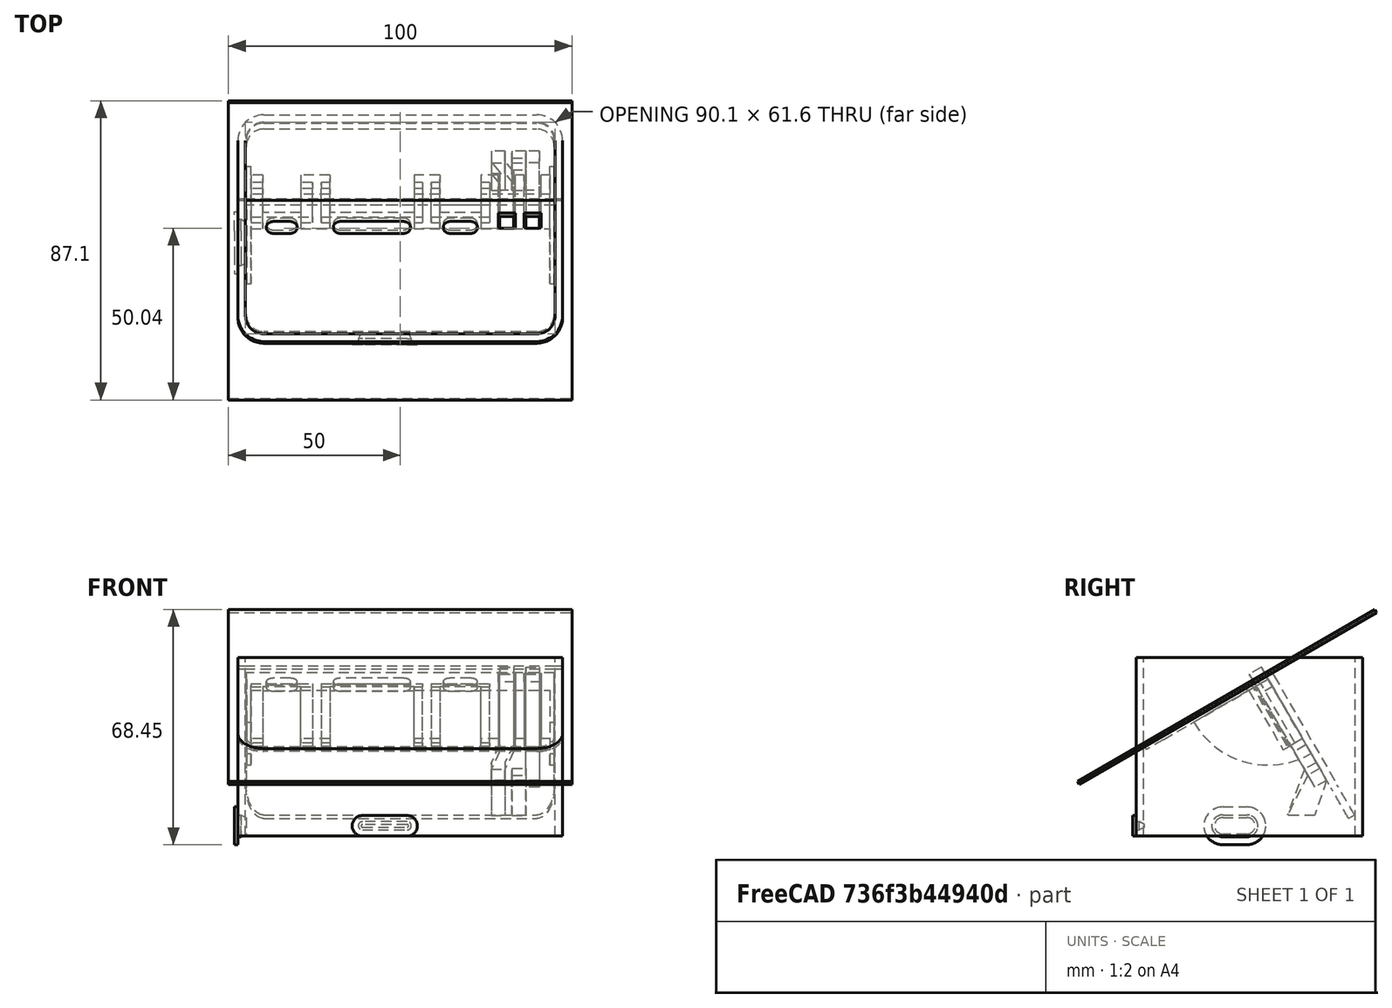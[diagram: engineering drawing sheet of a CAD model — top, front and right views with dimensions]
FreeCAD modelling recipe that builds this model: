
FCSTD DOCUMENT  (FreeCAD 0.21R33771 (Git))
Label: 2432S028_pins
License: All rights reserved
LicenseURL: http://en.wikipedia.org/wiki/All_rights_reserved
objects: Part::Extrusion×26, Sketcher::SketchObject×25, Part::FeaturePython×10, Part::Box×9, Part::Cut×7, Part::Chamfer×6, Mesh::Feature×6, Part::MultiCommon×1, Part::MultiFuse×1
note: 85 computed .brp shape members not serialized (recipe doc carries the construction recipe); baked Part::Feature solids carry a one-line shape summary decoded from their .brp

FEATURE [Sketcher::SketchObject] Sketch  label="Basis"
  FullyConstrained = true
  sketch-geometry (22):
    g0: LineSegment StartX=-39.75 StartY=33 StartZ=0 EndX=39.75 EndY=33 EndZ=0
    g1: LineSegment StartX=47.25 StartY=25.5 StartZ=0 EndX=47.25 EndY=-25.5 EndZ=0
    g2: LineSegment StartX=39.75 StartY=-33 StartZ=0 EndX=-39.75 EndY=-33 EndZ=0
    g3: LineSegment StartX=-47.25 StartY=-25.5 StartZ=0 EndX=-47.25 EndY=25.5 EndZ=0
    g4: ArcOfCircle CenterX=-39.75 CenterY=25.5 CenterZ=0 NormalX=0 NormalY=0 NormalZ=1 AngleXU=0 Radius=7.5 StartAngle=1.5708 EndAngle=3.14159
    g5: GeomPoint X=-47.25 Y=33 Z=0
    g6: ArcOfCircle CenterX=39.75 CenterY=25.5 CenterZ=0 NormalX=0 NormalY=0 NormalZ=1 AngleXU=0 Radius=7.5 StartAngle=0 EndAngle=1.5708
    g7: GeomPoint X=47.25 Y=33 Z=0
    g8: ArcOfCircle CenterX=39.75 CenterY=-25.5 CenterZ=0 NormalX=0 NormalY=0 NormalZ=1 AngleXU=0 Radius=7.5 StartAngle=4.71239 EndAngle=6.28319
    g9: GeomPoint X=47.25 Y=-33 Z=0
    g10: ArcOfCircle CenterX=-39.75 CenterY=-25.5 CenterZ=0 NormalX=0 NormalY=0 NormalZ=1 AngleXU=0 Radius=7.5 StartAngle=3.14159 EndAngle=4.71239
    g11: GeomPoint X=-47.25 Y=-33 Z=0
    g12: ArcOfCircle CenterX=39.75 CenterY=17.9 CenterZ=0 NormalX=0 NormalY=0 NormalZ=1 AngleXU=0 Radius=5.5 StartAngle=4e-16 EndAngle=1.5708
    g13: LineSegment StartX=45.25 StartY=17.9 StartZ=0 EndX=45.25 EndY=-25.5 EndZ=0
    g14: ArcOfCircle CenterX=39.75 CenterY=-25.5 CenterZ=0 NormalX=0 NormalY=0 NormalZ=1 AngleXU=0 Radius=5.5 StartAngle=4.71239 EndAngle=6.28319
    g15: LineSegment StartX=39.75 StartY=-31 StartZ=0 EndX=-39.75 EndY=-31 EndZ=0
    g16: ArcOfCircle CenterX=-39.75 CenterY=-25.5 CenterZ=0 NormalX=0 NormalY=0 NormalZ=1 AngleXU=0 Radius=5.5 StartAngle=3.14159 EndAngle=4.71239
    g17: LineSegment StartX=-45.25 StartY=-25.5 StartZ=0 EndX=-45.25 EndY=17.9 EndZ=0
    g18: ArcOfCircle CenterX=-39.75 CenterY=17.9 CenterZ=0 NormalX=0 NormalY=0 NormalZ=1 AngleXU=0 Radius=5.5 StartAngle=1.5708 EndAngle=3.14159
    g19: LineSegment StartX=-39.75 StartY=23.4 StartZ=0 EndX=39.75 EndY=23.4 EndZ=0
    g20: GeomPoint X=45.25 Y=23.4 Z=0
    g21: GeomPoint X=-45.25 Y=-31 Z=0
  constraints (50):
    c: Horizontal(g0)
    c: Horizontal(g2)
    c: Vertical(g1)
    c: Vertical(g3)
    c: DistanceY(g9,g7) = 66
    c: Symmetric(g5,g9,g-1)
    c: PointOnObject(g5,g0)
    c: PointOnObject(g5,g3)
    c: Tangent(g0,g4) = 1.5708
    c: Tangent(g3,g4) = 1.5708
    c: PointOnObject(g7,g0)
    c: PointOnObject(g7,g1)
    c: Tangent(g0,g6) = 1.5708
    c: Tangent(g1,g6) = 1.5708
    c: PointOnObject(g9,g1)
    c: PointOnObject(g9,g2)
    c: Tangent(g1,g8) = 1.5708
    c: Tangent(g2,g8) = 1.5708
    c: PointOnObject(g11,g2)
    c: PointOnObject(g11,g3)
    c: Tangent(g2,g10) = 1.5708
    c: Tangent(g3,g10) = 1.5708
    c: Equal(g8,g10)
    c: Equal(g10,g4)
    c: Equal(g4,g6)
    c: Tangent(g12,g13) = 1.5708
    c: Tangent(g13,g14) = 1.5708
    c: Tangent(g14,g15) = 1.5708
    c: Tangent(g15,g16) = 1.5708
    c: Tangent(g16,g17) = 1.5708
    c: Tangent(g17,g18) = 1.5708
    c: Tangent(g18,g19) = 1.5708
    c: Tangent(g19,g12) = 1.5708
    c: Horizontal(g15)
    c: Vertical(g13)
    c: Vertical(g17)
    c: Equal(g12,g14)
    c: Equal(g14,g16)
    c: Equal(g16,g18)
    c: PointOnObject(g20,g13)
    c: PointOnObject(g20,g19)
    c: PointOnObject(g21,g15)
    c: PointOnObject(g21,g17)
    c: DistanceY(g14,g12) = 54.4
    c: DistanceX(g17,g12) = 90.5
    c: Diameter(g12) = 11
    c: Symmetric(g12,g17,g-2)
    c: DistanceY(g2,g14) = 2
    c: Coincident(g10,g16)
    c: DistanceY(g18,g4) = 2.1
FEATURE [Part::Box] Box  label="Cube"
  AttacherType = Attacher::AttachEngine3D
  Height = 100
  Length = 100
  Placement = pos=(-50,39.3072,-0.4) rot=(1,0,0;0.523599rad)
  Width = 100
FEATURE [Sketcher::SketchObject] Sketch001
  ExternalGeometry = -> [Sketch]
  FullyConstrained = true
  sketch-geometry (20):
    g0: ArcOfCircle CenterX=-39.75 CenterY=25.5 CenterZ=0 NormalX=0 NormalY=0 NormalZ=1 AngleXU=0 Radius=7.5 StartAngle=1.5708 EndAngle=3.14159
    g1: LineSegment StartX=-39.75 StartY=33 StartZ=0 EndX=39.75 EndY=33 EndZ=0
    g2: ArcOfCircle CenterX=39.75 CenterY=25.5 CenterZ=0 NormalX=0 NormalY=0 NormalZ=1 AngleXU=0 Radius=7.5 StartAngle=1e-16 EndAngle=1.5708
    g3: LineSegment StartX=47.25 StartY=25.5 StartZ=0 EndX=47.25 EndY=-25.5 EndZ=0
    g4: ArcOfCircle CenterX=39.75 CenterY=-25.5 CenterZ=0 NormalX=0 NormalY=0 NormalZ=1 AngleXU=0 Radius=7.5 StartAngle=4.71239 EndAngle=6.28319
    g5: LineSegment StartX=39.75 StartY=-33 StartZ=0 EndX=-39.75 EndY=-33 EndZ=0
    g6: ArcOfCircle CenterX=-39.75 CenterY=-25.5 CenterZ=0 NormalX=0 NormalY=0 NormalZ=1 AngleXU=0 Radius=7.5 StartAngle=3.14159 EndAngle=4.71239
    g7: LineSegment StartX=-47.25 StartY=-25.5 StartZ=0 EndX=-47.25 EndY=25.5 EndZ=0
    g8: GeomPoint X=-47.25 Y=33 Z=0
    g9: GeomPoint X=47.25 Y=-33 Z=0
    g10: ArcOfCircle CenterX=-39.75 CenterY=17.9 CenterZ=0 NormalX=0 NormalY=0 NormalZ=1 AngleXU=0 Radius=5.5 StartAngle=1.5708 EndAngle=3.14159
    g11: LineSegment StartX=-39.75 StartY=23.4 StartZ=0 EndX=39.75 EndY=23.4 EndZ=0
    g12: ArcOfCircle CenterX=39.75 CenterY=17.9 CenterZ=0 NormalX=0 NormalY=0 NormalZ=1 AngleXU=0 Radius=5.5 StartAngle=0 EndAngle=1.5708
    g13: LineSegment StartX=45.25 StartY=17.9 StartZ=0 EndX=45.25 EndY=-25.5 EndZ=0
    g14: ArcOfCircle CenterX=39.75 CenterY=-25.5 CenterZ=0 NormalX=0 NormalY=0 NormalZ=1 AngleXU=0 Radius=5.5 StartAngle=4.71239 EndAngle=6.28319
    g15: LineSegment StartX=39.75 StartY=-31 StartZ=0 EndX=-39.75 EndY=-31 EndZ=0
    g16: ArcOfCircle CenterX=-39.75 CenterY=-25.5 CenterZ=0 NormalX=0 NormalY=0 NormalZ=1 AngleXU=0 Radius=5.5 StartAngle=3.14159 EndAngle=4.71239
    g17: LineSegment StartX=-45.25 StartY=-25.5 StartZ=0 EndX=-45.25 EndY=17.9 EndZ=0
    g18: GeomPoint X=-45.25 Y=23.4 Z=0
    g19: GeomPoint X=45.25 Y=-31 Z=0
  constraints (44):
    c: Tangent(g0,g1) = 1.5708
    c: Tangent(g1,g2) = 1.5708
    c: Tangent(g2,g3) = 1.5708
    c: Tangent(g3,g4) = 1.5708
    c: Tangent(g4,g5) = 1.5708
    c: Tangent(g5,g6) = 1.5708
    c: Tangent(g6,g7) = 1.5708
    c: Tangent(g7,g0) = 1.5708
    c: Horizontal(g1)
    c: Horizontal(g5)
    c: Vertical(g3)
    c: Vertical(g7)
    c: Equal(g0,g2)
    c: Equal(g2,g4)
    c: Equal(g4,g6)
    c: PointOnObject(g8,g1)
    c: PointOnObject(g8,g7)
    c: PointOnObject(g9,g3)
    c: PointOnObject(g9,g5)
    c: Coincident(g-6,g4)
    c: Coincident(g0,g-3)
    c: Horizontal(g-3,g0)
    c: Tangent(g10,g11) = 1.5708
    c: Tangent(g11,g12) = 1.5708
    c: Tangent(g12,g13) = 1.5708
    c: Tangent(g13,g14) = 1.5708
    c: Tangent(g14,g15) = 1.5708
    c: Tangent(g15,g16) = 1.5708
    c: Tangent(g16,g17) = 1.5708
    c: Tangent(g17,g10) = 1.5708
    c: Horizontal(g11)
    c: Horizontal(g15)
    c: Vertical(g13)
    c: Vertical(g17)
    c: Equal(g10,g12)
    c: Equal(g12,g14)
    c: Equal(g14,g16)
    c: PointOnObject(g18,g11)
    c: PointOnObject(g18,g17)
    c: PointOnObject(g19,g13)
    c: PointOnObject(g19,g15)
    c: Coincident(g14,g4)
    c: Coincident(g10,g-5)
    c: Horizontal(g-5,g10)
FEATURE [Part::Extrusion] Extrude
  Base = -> Sketch001
  Dir = (0,0,1)
  DirMode = 2
  FaceMakerClass = Part::FaceMakerBullseye
  LengthFwd = 2
  LengthRev = 0
  Solid = true
  Symmetric = false
FEATURE [Sketcher::SketchObject] Sketch002
  ExternalGeometry = -> [Sketch]
  FullyConstrained = true
  Placement = pos=(0,0,2) rot=(0,0,1;0rad)
  sketch-geometry (26):
    g0: ArcOfCircle CenterX=-39.75 CenterY=25.5 CenterZ=0 NormalX=0 NormalY=0 NormalZ=1 AngleXU=0 Radius=7.5 StartAngle=1.5708 EndAngle=3.14159
    g1: LineSegment StartX=-39.75 StartY=33 StartZ=0 EndX=39.75 EndY=33 EndZ=0
    g2: ArcOfCircle CenterX=39.75 CenterY=25.5 CenterZ=0 NormalX=0 NormalY=0 NormalZ=1 AngleXU=0 Radius=7.5 StartAngle=4e-16 EndAngle=1.5708
    g3: LineSegment StartX=47.25 StartY=25.5 StartZ=0 EndX=47.25 EndY=-25.5 EndZ=0
    g4: ArcOfCircle CenterX=39.75 CenterY=-25.5 CenterZ=0 NormalX=0 NormalY=0 NormalZ=1 AngleXU=0 Radius=7.5 StartAngle=4.71239 EndAngle=6.28319
    g5: LineSegment StartX=39.75 StartY=-33 StartZ=0 EndX=-39.75 EndY=-33 EndZ=0
    g6: ArcOfCircle CenterX=-39.75 CenterY=-25.5 CenterZ=0 NormalX=0 NormalY=0 NormalZ=1 AngleXU=0 Radius=7.5 StartAngle=3.14159 EndAngle=4.71239
    g7: LineSegment StartX=-47.25 StartY=-25.5 StartZ=0 EndX=-47.25 EndY=25.5 EndZ=0
    g8: GeomPoint X=-47.25 Y=33 Z=0
    g9: GeomPoint X=47.25 Y=-33 Z=0
    g10: ArcOfCircle CenterX=-39.75 CenterY=17.9 CenterZ=0 NormalX=0 NormalY=0 NormalZ=1 AngleXU=0 Radius=5.5 StartAngle=1.5708 EndAngle=3.14159
    g11: LineSegment StartX=-39.75 StartY=23.4 StartZ=0 EndX=39.75 EndY=23.4 EndZ=0
    g12: ArcOfCircle CenterX=39.75 CenterY=17.9 CenterZ=0 NormalX=0 NormalY=0 NormalZ=1 AngleXU=0 Radius=5.5 StartAngle=0 EndAngle=1.5708
    g13: LineSegment StartX=45.25 StartY=17.9 StartZ=0 EndX=45.25 EndY=-25.5 EndZ=0
    g14: ArcOfCircle CenterX=39.75 CenterY=-25.5 CenterZ=0 NormalX=0 NormalY=0 NormalZ=1 AngleXU=0 Radius=5.5 StartAngle=4.71239 EndAngle=6.28319
    g15: LineSegment StartX=39.75 StartY=-31 StartZ=0 EndX=-39.75 EndY=-31 EndZ=0
    g16: ArcOfCircle CenterX=-39.75 CenterY=-25.5 CenterZ=0 NormalX=0 NormalY=0 NormalZ=1 AngleXU=0 Radius=5.5 StartAngle=3.14159 EndAngle=4.71239
    g17: LineSegment StartX=-45.25 StartY=-25.5 StartZ=0 EndX=-45.25 EndY=17.9 EndZ=0
    g18: GeomPoint X=-45.25 Y=23.4 Z=0
    g19: GeomPoint X=45.25 Y=-31 Z=0
    g20: ArcOfCircle CenterX=-39.75 CenterY=25.5 CenterZ=0 NormalX=0 NormalY=0 NormalZ=1 AngleXU=0 Radius=5.5 StartAngle=1.5708 EndAngle=3.14159
    g21: LineSegment StartX=-39.75 StartY=31 StartZ=0 EndX=39.75 EndY=31 EndZ=0
    g22: ArcOfCircle CenterX=39.75 CenterY=25.5 CenterZ=0 NormalX=0 NormalY=0 NormalZ=1 AngleXU=0 Radius=5.5 StartAngle=0 EndAngle=1.5708
    g23: LineSegment StartX=-45.25 StartY=25.4 StartZ=0 EndX=45.25 EndY=25.4 EndZ=0
    g24: LineSegment StartX=-45.25 StartY=25.5 StartZ=0 EndX=-45.25 EndY=25.4 EndZ=0
    g25: LineSegment StartX=45.25 StartY=25.5 StartZ=0 EndX=45.25 EndY=25.4 EndZ=0
  constraints (62):
    c: Tangent(g0,g1) = 1.5708
    c: Tangent(g1,g2) = 1.5708
    c: Tangent(g2,g3) = 1.5708
    c: Tangent(g3,g4) = 1.5708
    c: Tangent(g4,g5) = 1.5708
    c: Tangent(g5,g6) = 1.5708
    c: Tangent(g6,g7) = 1.5708
    c: Tangent(g7,g0) = 1.5708
    c: Horizontal(g1)
    c: Horizontal(g5)
    c: Vertical(g3)
    c: Vertical(g7)
    c: Equal(g0,g2)
    c: Equal(g2,g4)
    c: Equal(g4,g6)
    c: PointOnObject(g8,g1)
    c: PointOnObject(g8,g7)
    c: PointOnObject(g9,g3)
    c: PointOnObject(g9,g5)
    c: Coincident(g4,g-6)
    c: Coincident(g0,g-3)
    c: Horizontal(g-3,g0)
    c: Tangent(g10,g11) = 1.5708
    c: Tangent(g11,g12) = 1.5708
    c: Tangent(g12,g13) = 1.5708
    c: Tangent(g13,g14) = 1.5708
    c: Tangent(g14,g15) = 1.5708
    c: Tangent(g15,g16) = 1.5708
    c: Tangent(g16,g17) = 1.5708
    c: Tangent(g17,g10) = 1.5708
    c: Horizontal(g11)
    c: Horizontal(g15)
    c: Vertical(g13)
    c: Vertical(g17)
    c: Equal(g10,g12)
    c: Equal(g12,g14)
    c: Equal(g14,g16)
    c: PointOnObject(g18,g11)
    c: PointOnObject(g18,g17)
    c: PointOnObject(g19,g13)
    c: PointOnObject(g19,g15)
    c: Coincident(g4,g14)
    c: Coincident(g10,g-5)
    c: Horizontal(g14,g-6)
    c: Coincident(g20,g0)
    c: Vertical(g0,g20)
    c: Horizontal(g0,g20)
    c: DistanceY(g20,g0) = 2
    c: Coincident(g21,g20)
    c: Horizontal(g21)
    c: Coincident(g22,g2)
    c: Coincident(g22,g21)
    c: Equal(g22,g20)
    c: Horizontal(g2,g22)
    c: Horizontal(g23)
    c: Coincident(g24,g20)
    c: Coincident(g24,g23)
    c: Vertical(g24)
    c: Coincident(g25,g22)
    c: Coincident(g25,g23)
    c: Vertical(g25)
    c: DistanceY(g10,g23) = 2
FEATURE [Part::Extrusion] Extrude001  label="Extrude_2mm"
  Base = -> Sketch002
  Dir = (0,0,1)
  DirMode = 2
  FaceMakerClass = Part::FaceMakerBullseye
  LengthFwd = 2
  LengthRev = 0
  Solid = true
  Symmetric = false
FEATURE [Sketcher::SketchObject] Sketch003
  ExternalGeometry = -> [Sketch]
  FullyConstrained = true
  Placement = pos=(0,0,4) rot=(0,0,1;0rad)
  sketch-geometry (20):
    g0: ArcOfCircle CenterX=-39.75 CenterY=25.5 CenterZ=0 NormalX=0 NormalY=0 NormalZ=1 AngleXU=0 Radius=7.5 StartAngle=1.5708 EndAngle=3.14159
    g1: LineSegment StartX=-39.75 StartY=33 StartZ=0 EndX=39.75 EndY=33 EndZ=0
    g2: ArcOfCircle CenterX=39.75 CenterY=25.5 CenterZ=0 NormalX=0 NormalY=0 NormalZ=1 AngleXU=0 Radius=7.5 StartAngle=0 EndAngle=1.5708
    g3: LineSegment StartX=47.25 StartY=25.5 StartZ=0 EndX=47.25 EndY=-25.5 EndZ=0
    g4: ArcOfCircle CenterX=39.75 CenterY=-25.5 CenterZ=0 NormalX=0 NormalY=0 NormalZ=1 AngleXU=0 Radius=7.5 StartAngle=4.71239 EndAngle=6.28319
    g5: LineSegment StartX=39.75 StartY=-33 StartZ=0 EndX=-39.75 EndY=-33 EndZ=0
    g6: ArcOfCircle CenterX=-39.75 CenterY=-25.5 CenterZ=0 NormalX=0 NormalY=0 NormalZ=1 AngleXU=0 Radius=7.5 StartAngle=3.14159 EndAngle=4.71239
    g7: LineSegment StartX=-47.25 StartY=-25.5 StartZ=0 EndX=-47.25 EndY=25.5 EndZ=0
    g8: GeomPoint X=-47.25 Y=33 Z=0
    g9: GeomPoint X=47.25 Y=-33 Z=0
    g10: ArcOfCircle CenterX=-39.75 CenterY=25.5 CenterZ=0 NormalX=0 NormalY=0 NormalZ=1 AngleXU=0 Radius=5.5 StartAngle=1.5708 EndAngle=3.14159
    g11: LineSegment StartX=-39.75 StartY=31 StartZ=0 EndX=39.75 EndY=31 EndZ=0
    g12: ArcOfCircle CenterX=39.75 CenterY=25.5 CenterZ=0 NormalX=0 NormalY=0 NormalZ=1 AngleXU=0 Radius=5.5 StartAngle=0 EndAngle=1.5708
    g13: LineSegment StartX=45.25 StartY=25.5 StartZ=0 EndX=45.25 EndY=-25.5 EndZ=0
    g14: ArcOfCircle CenterX=39.75 CenterY=-25.5 CenterZ=0 NormalX=0 NormalY=0 NormalZ=1 AngleXU=0 Radius=5.5 StartAngle=4.71239 EndAngle=6.28319
    g15: LineSegment StartX=39.75 StartY=-31 StartZ=0 EndX=-39.75 EndY=-31 EndZ=0
    g16: ArcOfCircle CenterX=-39.75 CenterY=-25.5 CenterZ=0 NormalX=0 NormalY=0 NormalZ=1 AngleXU=0 Radius=5.5 StartAngle=3.14159 EndAngle=4.71239
    g17: LineSegment StartX=-45.25 StartY=-25.5 StartZ=0 EndX=-45.25 EndY=25.5 EndZ=0
    g18: GeomPoint X=-45.25 Y=31 Z=0
    g19: GeomPoint X=45.25 Y=-31 Z=0
  constraints (45):
    c: Tangent(g0,g1) = 1.5708
    c: Tangent(g1,g2) = 1.5708
    c: Tangent(g2,g3) = 1.5708
    c: Tangent(g3,g4) = 1.5708
    c: Tangent(g4,g5) = 1.5708
    c: Tangent(g5,g6) = 1.5708
    c: Tangent(g6,g7) = 1.5708
    c: Tangent(g7,g0) = 1.5708
    c: Horizontal(g1)
    c: Horizontal(g5)
    c: Vertical(g3)
    c: Vertical(g7)
    c: Equal(g0,g2)
    c: Equal(g2,g4)
    c: Equal(g4,g6)
    c: PointOnObject(g8,g1)
    c: PointOnObject(g8,g7)
    c: PointOnObject(g9,g3)
    c: PointOnObject(g9,g5)
    c: Coincident(g-5,g4)
    c: Coincident(g0,g-3)
    c: Horizontal(g-3,g0)
    c: Tangent(g10,g11) = 1.5708
    c: Tangent(g12,g13) = 1.5708
    c: Tangent(g13,g14) = 1.5708
    c: Tangent(g14,g15) = 1.5708
    c: Tangent(g15,g16) = 1.5708
    c: Tangent(g16,g17) = 1.5708
    c: Tangent(g17,g10) = 1.5708
    c: Horizontal(g11)
    c: Horizontal(g15)
    c: Vertical(g13)
    c: Vertical(g17)
    c: Equal(g10,g12)
    c: Equal(g12,g14)
    c: Equal(g14,g16)
    c: PointOnObject(g18,g11)
    c: PointOnObject(g18,g17)
    c: PointOnObject(g19,g13)
    c: PointOnObject(g19,g15)
    c: Coincident(g14,g4)
    c: Coincident(g11,g12)
    c: Coincident(g0,g10)
    c: Horizontal(g15,g-6)
    c: Vertical(g12,g11)
FEATURE [Part::Extrusion] Extrude002  label="Extrude_4mm"
  Base = -> Sketch003
  Dir = (0,0,1)
  DirMode = 2
  FaceMakerClass = Part::FaceMakerBullseye
  LengthFwd = 10
  LengthRev = 0
  Solid = true
  Symmetric = false
FEATURE [Part::Extrusion] Extrude003  label="Extrude_6mm"
  Base = -> Sketch003
  Dir = (0,0,1)
  DirMode = 2
  FaceMakerClass = Part::FaceMakerBullseye
  LengthFwd = 52
  LengthRev = 0
  Solid = true
  Symmetric = false
FEATURE [Part::Box] Box001  label="Cube001"
  AttacherType = Attacher::AttachEngine3D
  Height = 100
  Length = 100
  Placement = pos=(-50,-49.5397,19.0874) rot=(1,0,0;0.523599rad)
  Width = 100
FEATURE [Part::Box] Box002  label="Cube002"
  AttacherType = Attacher::AttachEngine3D
  Height = 100
  Length = 100
  Placement = pos=(-50,37.5751,-1.4) rot=(1,0,0;0.523599rad)
  Width = 2
FEATURE [Sketcher::SketchObject] Sketch004
  ExternalGeometry = -> [Sketch]
  FullyConstrained = false
  sketch-geometry (12):
    g0: ArcOfCircle CenterX=-39.75 CenterY=25.5 CenterZ=0 NormalX=0 NormalY=0 NormalZ=1 AngleXU=0 Radius=7.5 StartAngle=1.5708 EndAngle=3.14159
    g1: LineSegment StartX=-39.75 StartY=33 StartZ=0 EndX=39.75 EndY=33 EndZ=0
    g2: ArcOfCircle CenterX=39.75 CenterY=25.5 CenterZ=0 NormalX=0 NormalY=0 NormalZ=1 AngleXU=0 Radius=7.5 StartAngle=1e-16 EndAngle=1.5708
    g3: LineSegment StartX=47.25 StartY=25.5 StartZ=0 EndX=47.25 EndY=-25.5 EndZ=0
    g4: ArcOfCircle CenterX=39.75 CenterY=-25.5 CenterZ=0 NormalX=0 NormalY=0 NormalZ=1 AngleXU=0 Radius=7.5 StartAngle=4.71239 EndAngle=6.28319
    g5: LineSegment StartX=39.75 StartY=-33 StartZ=0 EndX=-39.75 EndY=-33 EndZ=0
    g6: ArcOfCircle CenterX=-39.75 CenterY=-25.5 CenterZ=0 NormalX=0 NormalY=0 NormalZ=1 AngleXU=0 Radius=7.5 StartAngle=3.14159 EndAngle=4.71239
    g7: LineSegment StartX=-47.25 StartY=-25.5 StartZ=0 EndX=-47.25 EndY=25.5 EndZ=0
    g8: GeomPoint X=-47.25 Y=33 Z=0
    g9: GeomPoint X=47.25 Y=-33 Z=0
    g10: GeomPoint X=-22 Y=14 Z=0
    g11: GeomPoint X=22 Y=-30 Z=0
  constraints (22):
    c: Tangent(g0,g1) = 1.5708
    c: Tangent(g1,g2) = 1.5708
    c: Tangent(g2,g3) = 1.5708
    c: Tangent(g3,g4) = 1.5708
    c: Tangent(g4,g5) = 1.5708
    c: Tangent(g5,g6) = 1.5708
    c: Tangent(g6,g7) = 1.5708
    c: Tangent(g7,g0) = 1.5708
    c: Horizontal(g1)
    c: Horizontal(g5)
    c: Vertical(g3)
    c: Vertical(g7)
    c: Equal(g0,g2)
    c: Equal(g2,g4)
    c: Equal(g4,g6)
    c: PointOnObject(g8,g1)
    c: PointOnObject(g8,g7)
    c: PointOnObject(g9,g3)
    c: PointOnObject(g9,g5)
    c: Coincident(g0,g-3)
    c: Horizontal(g-3,g0)
    c: Coincident(g4,g-4)
FEATURE [Part::Extrusion] Extrude004
  Base = -> Sketch004
  Dir = (0,0,1)
  DirMode = 2
  FaceMakerClass = Part::FaceMakerBullseye
  LengthFwd = 56
  LengthRev = 0
  Solid = true
  Symmetric = false
FEATURE [Part::MultiCommon] Common
  Shapes = -> [Box002,Extrude004]
FEATURE [Part::MultiFuse] Fusion
  Shapes = -> [Common,Extrude,Extrude001,Extrude002,Extrude003]
FEATURE [Part::Cut] Cut
  Base = -> Fusion
  Tool = -> Box
FEATURE [Part::Cut] Cut001
  Base = -> Cut
  Tool = -> Box001
FEATURE [Part::Box] Box003  label="Cube003"
  AttacherType = Attacher::AttachEngine3D
  Height = 3
  Length = 1.5
  Placement = pos=(43.75,-29,7) rot=(0,0,1;0rad)
  Width = 14.7
FEATURE [Part::Chamfer] Chamfer
  Base = -> Box003
  Edges = 4 edges r=1.49: [Edge1,Edge2,Edge3,Edge4]
FEATURE [Part::Box] Box004  label="Cube004"
  AttacherType = Attacher::AttachEngine3D
  Height = 3
  Length = 1.5
  Placement = pos=(-45.25,-29,8) rot=(0,0,1;0rad)
  Width = 14.7
FEATURE [Part::Chamfer] Chamfer001
  Base = -> Box004
  Edges = 4 edges r=1.49: [Edge5,Edge6,Edge7,Edge8]
FEATURE [Sketcher::SketchObject] Sketch005  label="Basis001_bEZEL"
  FullyConstrained = true
  Placement = pos=(0,-2.75,0) rot=(0,1,0;3.14159rad)
  sketch-geometry (46):
    g0: ArcOfCircle CenterX=40 CenterY=22 CenterZ=0 NormalX=0 NormalY=0 NormalZ=1 AngleXU=0 Radius=3 StartAngle=4e-16 EndAngle=1.5708
    g1: LineSegment StartX=43 StartY=22 StartZ=0 EndX=43 EndY=-22 EndZ=0
    g2: ArcOfCircle CenterX=40 CenterY=-22 CenterZ=0 NormalX=0 NormalY=0 NormalZ=1 AngleXU=0 Radius=3 StartAngle=4.71239 EndAngle=6.28319
    g3: LineSegment StartX=40 StartY=-25 StartZ=0 EndX=-40 EndY=-25 EndZ=0
    g4: ArcOfCircle CenterX=-40 CenterY=-22 CenterZ=0 NormalX=0 NormalY=0 NormalZ=1 AngleXU=0 Radius=3 StartAngle=3.14159 EndAngle=4.71239
    g5: LineSegment StartX=-43 StartY=-22 StartZ=0 EndX=-43 EndY=22 EndZ=0
    g6: ArcOfCircle CenterX=-40 CenterY=22 CenterZ=0 NormalX=0 NormalY=0 NormalZ=1 AngleXU=0 Radius=3 StartAngle=1.5708 EndAngle=3.14159
    g7: LineSegment StartX=-40 StartY=25 StartZ=0 EndX=40 EndY=25 EndZ=0
    g8: GeomPoint X=43 Y=25 Z=0
    g9: GeomPoint X=-43 Y=-25 Z=0
    g10: Circle CenterX=-39 CenterY=21 CenterZ=0 NormalX=0 NormalY=0 NormalZ=1 AngleXU=0 Radius=1.6
    g11: Circle CenterX=-39 CenterY=-21 CenterZ=0 NormalX=0 NormalY=0 NormalZ=1 AngleXU=0 Radius=1.6
    g12: Circle CenterX=39 CenterY=21 CenterZ=0 NormalX=0 NormalY=0 NormalZ=1 AngleXU=0 Radius=1.6
    g13: Circle CenterX=39 CenterY=-21 CenterZ=0 NormalX=0 NormalY=0 NormalZ=1 AngleXU=0 Radius=1.6
    g14: LineSegment StartX=-35 StartY=25 StartZ=0 EndX=36 EndY=25 EndZ=0
    g15: LineSegment StartX=36 StartY=25 StartZ=0 EndX=36 EndY=-25 EndZ=0
    g16: LineSegment StartX=36 StartY=-25 StartZ=0 EndX=-35 EndY=-25 EndZ=0
    g17: LineSegment StartX=-35 StartY=-25 StartZ=0 EndX=-35 EndY=25 EndZ=0
    g18: LineSegment StartX=-40.4 StartY=-12 StartZ=0 EndX=-37.4 EndY=-12 EndZ=0
    g19: LineSegment StartX=-37.4 StartY=-12 StartZ=0 EndX=-37.4 EndY=-17 EndZ=0
    g20: LineSegment StartX=-37.4 StartY=-17 StartZ=0 EndX=-40.4 EndY=-17 EndZ=0
    g21: LineSegment StartX=-40.4 StartY=-17 StartZ=0 EndX=-40.4 EndY=-12 EndZ=0
    g22: LineSegment StartX=-2 StartY=-25 StartZ=0 EndX=11 EndY=-25 EndZ=0
    g23: LineSegment StartX=11 StartY=-25 StartZ=0 EndX=11 EndY=-28 EndZ=0
    g24: LineSegment StartX=11 StartY=-28 StartZ=0 EndX=-2 EndY=-28 EndZ=0
    g25: LineSegment StartX=-2 StartY=-28 StartZ=0 EndX=-2 EndY=-25 EndZ=0
    g26: LineSegment StartX=43 StartY=3 StartZ=0 EndX=53 EndY=3 EndZ=0
    g27: LineSegment StartX=53 StartY=3 StartZ=0 EndX=53 EndY=-6 EndZ=0
    g28: LineSegment StartX=53 StartY=-6 StartZ=0 EndX=43 EndY=-6 EndZ=0
    g29: LineSegment StartX=43 StartY=-6 StartZ=0 EndX=43 EndY=3 EndZ=0
    g30: LineSegment StartX=43 StartY=14 StartZ=0 EndX=45 EndY=14 EndZ=0
    g31: LineSegment StartX=45 StartY=14 StartZ=0 EndX=45 EndY=6 EndZ=0
    g32: LineSegment StartX=45 StartY=6 StartZ=0 EndX=43 EndY=6 EndZ=0
    g33: LineSegment StartX=43 StartY=6 StartZ=0 EndX=43 EndY=14 EndZ=0
    g34: LineSegment StartX=-31.5 StartY=-25 StartZ=0 EndX=-23.5 EndY=-25 EndZ=0
    g35: LineSegment StartX=-23.5 StartY=-25 StartZ=0 EndX=-23.5 EndY=-27 EndZ=0
    g36: LineSegment StartX=-23.5 StartY=-27 StartZ=0 EndX=-31.5 EndY=-27 EndZ=0
    g37: LineSegment StartX=-31.5 StartY=-27 StartZ=0 EndX=-31.5 EndY=-25 EndZ=0
    g38: LineSegment StartX=-16.5 StartY=-25 StartZ=0 EndX=-8.5 EndY=-25 EndZ=0
    g39: LineSegment StartX=-8.5 StartY=-25 StartZ=0 EndX=-8.5 EndY=-27 EndZ=0
    g40: LineSegment StartX=-8.5 StartY=-27 StartZ=0 EndX=-16.5 EndY=-27 EndZ=0
    g41: LineSegment StartX=-16.5 StartY=-27 StartZ=0 EndX=-16.5 EndY=-25 EndZ=0
    g42: LineSegment StartX=-33 StartY=22.5 StartZ=0 EndX=27 EndY=22.5 EndZ=0
    g43: LineSegment StartX=27 StartY=22.5 StartZ=0 EndX=27 EndY=-22.5 EndZ=0
    g44: LineSegment StartX=27 StartY=-22.5 StartZ=0 EndX=-33 EndY=-22.5 EndZ=0
    g45: LineSegment StartX=-33 StartY=-22.5 StartZ=0 EndX=-33 EndY=22.5 EndZ=0
  constraints (130):
    c: Tangent(g0,g1) = 1.5708
    c: Tangent(g1,g2) = 1.5708
    c: Tangent(g2,g3) = 1.5708
    c: Tangent(g3,g4) = 1.5708
    c: Tangent(g4,g5) = 1.5708
    c: Tangent(g5,g6) = 1.5708
    c: Tangent(g6,g7) = 1.5708
    c: Tangent(g7,g0) = 1.5708
    c: Horizontal(g3)
    c: Vertical(g1)
    c: Vertical(g5)
    c: Equal(g0,g2)
    c: Equal(g2,g4)
    c: Equal(g4,g6)
    c: PointOnObject(g8,g1)
    c: PointOnObject(g8,g7)
    c: PointOnObject(g9,g3)
    c: PointOnObject(g9,g5)
    c: DistanceY(g2,g0) = 50
    c: DistanceX(g5,g0) = 86
    c: Diameter(g0) = 6
    c: Symmetric(g6,g2,g-1)
    c: Horizontal(g7)
    c: Diameter(g10) = 3.2
    c: DistanceY(g10,g6) = 4
    c: DistanceX(g5,g10) = 4
    c: Equal(g10,g12)
    c: Horizontal(g10,g12)
    c: Vertical(g10,g11)
    c: Horizontal(g11,g13)
    c: Vertical(g13,g12)
    c: Equal(g10,g11)
    c: Equal(g11,g13)
    c: DistanceY(g2,g13) = 4
    c: DistanceX(g13,g1) = 4
    c: Coincident(g14,g15)
    c: Coincident(g15,g16)
    c: Coincident(g16,g17)
    c: Coincident(g17,g14)
    c: Horizontal(g14)
    c: Horizontal(g16)
    c: Vertical(g15)
    c: Vertical(g17)
    c: PointOnObject(g14,g7)
    c: PointOnObject(g16,g3)
    c: DistanceX(g14,g0) = 7
    c: DistanceX(g5,g14) = 8
    c: Coincident(g18,g19)
    c: Coincident(g19,g20)
    c: Coincident(g20,g21)
    c: Coincident(g21,g18)
    c: Horizontal(g18)
    c: Horizontal(g20)
    c: Vertical(g19)
    c: Vertical(g21)
    c: DistanceX(g20,g20) = 3
    c: DistanceY(g21,g21) = 5
    c: DistanceY(g3,g20) = 8
    c: DistanceX(g4,g20) = 2.6
    c: Coincident(g22,g23)
    c: Coincident(g23,g24)
    c: Coincident(g24,g25)
    c: Coincident(g25,g22)
    c: Horizontal(g22)
    c: Horizontal(g24)
    c: Vertical(g23)
    c: Vertical(g25)
    c: PointOnObject(g22,g3)
    c: DistanceX(g4,g22) = 41
    c: DistanceX(g22,g1) = 32
    c: DistanceY(g23,g23) = 3
    c: Coincident(g26,g27)
    c: Coincident(g27,g28)
    c: Coincident(g28,g29)
    c: Coincident(g29,g26)
    c: Horizontal(g26)
    c: Horizontal(g28)
    c: Vertical(g27)
    c: Vertical(g29)
    c: PointOnObject(g26,g1)
    c: DistanceY(g26,g0) = 22
    c: DistanceY(g2,g28) = 19
    c: DistanceX(g26,g26) = 10
    c: Coincident(g30,g31)
    c: Coincident(g31,g32)
    c: Coincident(g32,g33)
    c: Coincident(g33,g30)
    c: Horizontal(g30)
    c: Horizontal(g32)
    c: Vertical(g31)
    c: Vertical(g33)
    c: PointOnObject(g30,g1)
    c: DistanceY(g30,g0) = 11
    c: DistanceY(g2,g32) = 31
    c: DistanceX(g30,g30) = 2
    c: Coincident(g34,g35)
    c: Coincident(g35,g36)
    c: Coincident(g36,g37)
    c: Coincident(g37,g34)
    c: Horizontal(g34)
    c: Horizontal(g36)
    c: Vertical(g35)
    c: Vertical(g37)
    c: PointOnObject(g34,g3)
    c: Coincident(g38,g39)
    c: Coincident(g39,g40)
    c: Coincident(g40,g41)
    c: Coincident(g41,g38)
    c: Horizontal(g38)
    c: Horizontal(g40)
    c: Vertical(g39)
    c: Vertical(g41)
    c: PointOnObject(g38,g3)
    c: Equal(g31,g40)
    c: Equal(g40,g36)
    c: Equal(g32,g39)
    c: Equal(g39,g35)
    c: DistanceX(g4,g34) = 11.5
    c: DistanceX(g4,g38) = 26.5
    c: Coincident(g42,g43)
    c: Coincident(g43,g44)
    c: Coincident(g44,g45)
    c: Coincident(g45,g42)
    c: Horizontal(g42)
    c: Horizontal(g44)
    c: Vertical(g43)
    c: DistanceX(g44,g44) = 60
    c: DistanceY(g43,g43) = 45
    c: Symmetric(g42,g44,g-1)
    c: DistanceX(g14,g42) = 2
FEATURE [Sketcher::SketchObject] Sketch006
  ExternalGeometry = -> [Sketch005]
  FullyConstrained = true
  MapMode = 5
  Placement = pos=(0,-33,0) rot=(1,0,0;1.5708rad)
  Support = -> [Cut001]
  sketch-geometry (4):
    g0: ArcOfCircle CenterX=2 CenterY=7 CenterZ=0 NormalX=0 NormalY=0 NormalZ=1 AngleXU=0 Radius=1.5 StartAngle=4.71239 EndAngle=7.85398
    g1: ArcOfCircle CenterX=-11 CenterY=7 CenterZ=0 NormalX=0 NormalY=0 NormalZ=1 AngleXU=0 Radius=1.5 StartAngle=1.5708 EndAngle=4.71239
    g2: LineSegment StartX=2 StartY=8.5 StartZ=0 EndX=-11 EndY=8.5 EndZ=0
    g3: LineSegment StartX=-11 StartY=5.5 StartZ=0 EndX=2 EndY=5.5 EndZ=0
  constraints (10):
    c: Tangent(g0,g2) = -1.5708
    c: Tangent(g2,g1) = -1.5708
    c: Tangent(g1,g3) = -1.5708
    c: Tangent(g3,g0) = -1.5708
    c: Equal(g0,g1)
    c: Horizontal(g2)
    c: DistanceY(g-1,g1) = 7
    c: Diameter(g1) = 3
    c: Vertical(g1,g-3)
    c: Vertical(g0,g-3)
FEATURE [Part::Extrusion] Extrude005
  Base = -> Sketch006
  Dir = (0,-1,2e-16)
  DirMode = 2
  FaceMakerClass = Part::FaceMakerBullseye
  LengthFwd = 3
  LengthRev = 0
  Reversed = true
  Solid = true
  Symmetric = false
FEATURE [Sketcher::SketchObject] Sketch007
  ExternalGeometry = -> [Sketch005]
  FullyConstrained = true
  MapMode = 5
  Placement = pos=(-47.25,0,0) rot=(0.57735,-0.57735,-0.57735;2.0944rad)
  Support = -> [Cut001]
  sketch-geometry (6):
    g0: ArcOfCircle CenterX=0.75 CenterY=7 CenterZ=0 NormalX=0 NormalY=0 NormalZ=1 AngleXU=0 Radius=3.5 StartAngle=1.5708 EndAngle=4.71239
    g1: ArcOfCircle CenterX=7.75 CenterY=7 CenterZ=0 NormalX=0 NormalY=0 NormalZ=1 AngleXU=0 Radius=3.5 StartAngle=4.71239 EndAngle=7.85398
    g2: LineSegment StartX=0.75 StartY=3.5 StartZ=0 EndX=7.75 EndY=3.5 EndZ=0
    g3: LineSegment StartX=7.75 StartY=10.5 StartZ=0 EndX=0.75 EndY=10.5 EndZ=0
    g4: LineSegment StartX=-0.25 StartY=-6.5e-15 StartZ=0 EndX=0.75 EndY=3.5 EndZ=0
    g5: LineSegment StartX=7.75 StartY=3.5 StartZ=0 EndX=8.75 EndY=-6.7e-15 EndZ=0
  constraints (14):
    c: Tangent(g0,g2) = -1.5708
    c: Tangent(g2,g1) = -1.5708
    c: Tangent(g1,g3) = -1.5708
    c: Tangent(g3,g0) = -1.5708
    c: Equal(g0,g1)
    c: Horizontal(g2)
    c: DistanceY(g-1,g1) = 7
    c: Diameter(g1) = 7
    c: DistanceX(g3,g3) = 7
    c: Coincident(g4,g-3)
    c: Coincident(g4,g0)
    c: Coincident(g5,g1)
    c: Coincident(g5,g-3)
    c: Equal(g5,g4)
FEATURE [Part::Extrusion] Extrude006
  Base = -> Sketch007
  Dir = (-1,0,0)
  DirMode = 2
  FaceMakerClass = Part::FaceMakerBullseye
  LengthFwd = 3
  LengthRev = 0
  Reversed = true
  Solid = true
  Symmetric = false
FEATURE [Part::Box] Box005  label="Cube005"
  AttacherType = Attacher::AttachEngine3D
  Height = 3
  Length = 1.5
  Placement = pos=(43.75,10,7) rot=(0,0,1;0rad)
  Width = 14.7
FEATURE [Part::Chamfer] Chamfer002
  Base = -> Box005
  Edges = 4 edges r=1.49: [Edge1,Edge2,Edge3,Edge4]
FEATURE [Part::Box] Box006  label="Cube006"
  AttacherType = Attacher::AttachEngine3D
  Height = 3
  Length = 1.5
  Placement = pos=(-45.25,10,8) rot=(0,0,1;0rad)
  Width = 14.7
FEATURE [Part::Chamfer] Chamfer003
  Base = -> Box006
  Edges = 4 edges r=1.49: [Edge5,Edge6,Edge7,Edge8]
FEATURE [Part::Cut] Cut002
  Base = -> Cut001
  Tool = -> Extrude005
FEATURE [Part::Cut] Cut003
  Base = -> Cut002
  Tool = -> Extrude006
FEATURE [Part::FeaturePython] Connect  label="Main"  # WARN: FeaturePython — macro-defined, semantics opaque (R4)
  Objects = -> [Chamfer,Chamfer001,Chamfer002,Chamfer003,Cut003]
  Tolerance = 0
FEATURE [Mesh::Feature] Mesh  label="Main (Meshed)"
FEATURE [Sketcher::SketchObject] Sketch008
  ExternalGeometry = -> [Sketch007]
  FullyConstrained = true
  MapMode = 2
  Placement = pos=(-47.25,0,0) rot=(0.57735,-0.57735,-0.57735;2.0944rad)
  Support = -> [Sketch007]
  sketch-geometry (4):
    g0: ArcOfCircle CenterX=0.75 CenterY=7 CenterZ=0 NormalX=0 NormalY=0 NormalZ=1 AngleXU=0 Radius=3.2 StartAngle=1.5708 EndAngle=4.71239
    g1: ArcOfCircle CenterX=7.75 CenterY=7 CenterZ=0 NormalX=0 NormalY=0 NormalZ=1 AngleXU=0 Radius=3.2 StartAngle=4.71239 EndAngle=7.85398
    g2: LineSegment StartX=0.75 StartY=3.8 StartZ=0 EndX=7.75 EndY=3.8 EndZ=0
    g3: LineSegment StartX=7.75 StartY=10.2 StartZ=0 EndX=0.75 EndY=10.2 EndZ=0
  constraints (9):
    c: Radius(g-3) = 3.5
    c: Tangent(g0,g2) = -1.5708
    c: Tangent(g2,g1) = -1.5708
    c: Tangent(g1,g3) = -1.5708
    c: Tangent(g3,g0) = -1.5708
    c: Equal(g0,g1)
    c: Coincident(g0,g-3)
    c: Coincident(g1,g-4)
    c: Radius(g0) = 3.2
FEATURE [Part::Extrusion] Extrude007
  Base = -> Sketch008
  Dir = (-1,0,0)
  DirMode = 2
  FaceMakerClass = Part::FaceMakerBullseye
  LengthFwd = 2.4
  LengthRev = 0
  Reversed = true
  Solid = true
  Symmetric = false
FEATURE [Part::Chamfer] Chamfer004
  Base = -> Extrude007
  Edges = 1 edges: [Edge7 r1=1.5 r2=0.8]
FEATURE [Sketcher::SketchObject] Sketch009
  ExternalGeometry = -> [Sketch007]
  FullyConstrained = true
  MapMode = 2
  Placement = pos=(-47.25,0,0) rot=(0.57735,-0.57735,-0.57735;2.0944rad)
  Support = -> [Sketch007]
  sketch-geometry (4):
    g0: ArcOfCircle CenterX=0.75 CenterY=7 CenterZ=0 NormalX=0 NormalY=0 NormalZ=1 AngleXU=0 Radius=5.5 StartAngle=1.5708 EndAngle=4.71239
    g1: ArcOfCircle CenterX=7.75 CenterY=7 CenterZ=0 NormalX=0 NormalY=0 NormalZ=1 AngleXU=0 Radius=5.5 StartAngle=4.71239 EndAngle=7.85398
    g2: LineSegment StartX=0.75 StartY=1.5 StartZ=0 EndX=7.75 EndY=1.5 EndZ=0
    g3: LineSegment StartX=7.75 StartY=12.5 StartZ=0 EndX=0.75 EndY=12.5 EndZ=0
  constraints (9):
    c: Radius(g-3) = 3.5
    c: Tangent(g0,g2) = -1.5708
    c: Tangent(g2,g1) = -1.5708
    c: Tangent(g1,g3) = -1.5708
    c: Tangent(g3,g0) = -1.5708
    c: Equal(g0,g1)
    c: Coincident(g0,g-3)
    c: Coincident(g1,g-4)
    c: Radius(g0) = 5.5
FEATURE [Part::Extrusion] Extrude008
  Base = -> Sketch009
  Dir = (-1,0,0)
  DirMode = 2
  FaceMakerClass = Part::FaceMakerBullseye
  LengthFwd = 1
  LengthRev = 0
  Solid = true
  Symmetric = false
FEATURE [Part::FeaturePython] Connect001  label="Deckel_USB"  # WARN: FeaturePython — macro-defined, semantics opaque (R4)
  Objects = -> [Chamfer004,Extrude008]
  Tolerance = 0
FEATURE [Mesh::Feature] Mesh001  label="Deckel_USB (Meshed)"
  Placement = pos=(-57.5,0,48.25) rot=(0,1,0;4.71239rad)
FEATURE [Sketcher::SketchObject] Sketch010
  ExternalGeometry = -> [Sketch006]
  FullyConstrained = true
  MapMode = 2
  Placement = pos=(0,-33,0) rot=(1,0,0;1.5708rad)
  Support = -> [Sketch006]
  sketch-geometry (4):
    g0: ArcOfCircle CenterX=-11 CenterY=7 CenterZ=0 NormalX=0 NormalY=0 NormalZ=1 AngleXU=0 Radius=1.2 StartAngle=1.5708 EndAngle=4.71239
    g1: ArcOfCircle CenterX=2 CenterY=7 CenterZ=0 NormalX=0 NormalY=0 NormalZ=1 AngleXU=0 Radius=1.2 StartAngle=4.71239 EndAngle=7.85398
    g2: LineSegment StartX=-11 StartY=5.8 StartZ=0 EndX=2 EndY=5.8 EndZ=0
    g3: LineSegment StartX=2 StartY=8.2 StartZ=0 EndX=-11 EndY=8.2 EndZ=0
  constraints (9):
    c: Tangent(g0,g2) = -1.5708
    c: Tangent(g2,g1) = -1.5708
    c: Tangent(g1,g3) = -1.5708
    c: Tangent(g3,g0) = -1.5708
    c: Equal(g0,g1)
    c: Coincident(g0,g-3)
    c: Coincident(g1,g-4)
    c: Radius(g-3) = 1.5
    c: Radius(g0) = 1.2
FEATURE [Part::Extrusion] Extrude009
  Base = -> Sketch010
  Dir = (0,-1,2e-16)
  DirMode = 2
  FaceMakerClass = Part::FaceMakerBullseye
  LengthFwd = 2.4
  LengthRev = 0
  Reversed = true
  Solid = true
  Symmetric = false
FEATURE [Sketcher::SketchObject] Sketch011
  ExternalGeometry = -> [Sketch006]
  FullyConstrained = true
  MapMode = 2
  Placement = pos=(0,-33,0) rot=(1,0,0;1.5708rad)
  Support = -> [Sketch006]
  sketch-geometry (4):
    g0: ArcOfCircle CenterX=-11 CenterY=7 CenterZ=0 NormalX=0 NormalY=0 NormalZ=1 AngleXU=0 Radius=3 StartAngle=1.5708 EndAngle=4.71239
    g1: ArcOfCircle CenterX=2 CenterY=7 CenterZ=0 NormalX=0 NormalY=0 NormalZ=1 AngleXU=0 Radius=3 StartAngle=4.71239 EndAngle=7.85398
    g2: LineSegment StartX=-11 StartY=4 StartZ=0 EndX=2 EndY=4 EndZ=0
    g3: LineSegment StartX=2 StartY=10 StartZ=0 EndX=-11 EndY=10 EndZ=0
  constraints (9):
    c: Tangent(g0,g2) = -1.5708
    c: Tangent(g2,g1) = -1.5708
    c: Tangent(g1,g3) = -1.5708
    c: Tangent(g3,g0) = -1.5708
    c: Equal(g0,g1)
    c: Coincident(g0,g-3)
    c: Coincident(g1,g-4)
    c: Radius(g-3) = 1.5
    c: Radius(g0) = 3
FEATURE [Part::Extrusion] Extrude010
  Base = -> Sketch011
  Dir = (0,-1,2e-16)
  DirMode = 2
  FaceMakerClass = Part::FaceMakerBullseye
  LengthFwd = 1
  LengthRev = 0
  Solid = true
  Symmetric = false
FEATURE [Part::FeaturePython] Connect002  label="Deckel MicroSD"  # WARN: FeaturePython — macro-defined, semantics opaque (R4)
  Objects = -> [Extrude009,Extrude010]
  Tolerance = 0
FEATURE [Part::Chamfer] Chamfer005  label="Deckel MicroSD001"
  Base = -> Connect002
  Edges = 1 edges: [Edge11 r1=0.8 r2=1.5]
FEATURE [Mesh::Feature] Mesh003  label="Deckel MicroSD (Meshed)"
  Placement = pos=(0,-35.5,34) rot=(1,0,0;1.5708rad)
FEATURE [Part::Box] Box007  label="Cube007"
  AttacherType = Attacher::AttachEngine3D
  Height = 1
  Length = 100
  Placement = pos=(-50,-49.5397,19.0874) rot=(1,0,0;0.523599rad)
  Width = 100
FEATURE [Sketcher::SketchObject] Sketch012
  FullyConstrained = false
  Placement = pos=(0,-20.65,35.7668) rot=(1,0,0;3.66519rad)
  sketch-geometry (20):
    g0: LineSegment StartX=-47.25 StartY=5.6003 StartZ=0 EndX=-47.25 EndY=-31.841 EndZ=0
    g1: LineSegment StartX=-47.25 StartY=-31.841 StartZ=0 EndX=-47.25 EndY=-33.841 EndZ=0
    g2: LineSegment StartX=-47.25 StartY=-33.841 StartZ=0 EndX=-45.25 EndY=-33.841 EndZ=0
    g3: LineSegment StartX=-45.25 StartY=-33.841 StartZ=0 EndX=45.25 EndY=-33.841 EndZ=0
    g4: LineSegment StartX=45.25 StartY=-33.841 StartZ=0 EndX=47.25 EndY=-33.841 EndZ=0
    g5: LineSegment StartX=47.25 StartY=-33.841 StartZ=0 EndX=47.25 EndY=-31.841 EndZ=0
    g6: LineSegment StartX=47.25 StartY=-31.841 StartZ=0 EndX=47.25 EndY=5.6003 EndZ=0
    g7: ArcOfEllipse CenterX=39.75 CenterY=5.6003 CenterZ=0 NormalX=0 NormalY=-1e-16 NormalZ=1 MajorRadius=8.66025 MinorRadius=7.5 AngleXU=0 StartAngle=4.71239 EndAngle=6.28319
    g8: LineSegment StartX=39.75 StartY=14.2606 StartZ=0 EndX=-39.75 EndY=14.2606 EndZ=0
    g9: ArcOfEllipse CenterX=-39.75 CenterY=5.6003 CenterZ=0 NormalX=0 NormalY=-1e-16 NormalZ=1 MajorRadius=8.66025 MinorRadius=7.5 AngleXU=0 StartAngle=0 EndAngle=1.5708
    g10: ArcOfEllipse CenterX=-39.7356 CenterY=5.58989 CenterZ=0 NormalX=0 NormalY=-1e-16 NormalZ=1 MajorRadius=6.36708 MinorRadius=5.51431 AngleXU=0.0120287 StartAngle=6.27107 EndAngle=7.8407
    g11: LineSegment StartX=39.75 StartY=11.9568 StartZ=0 EndX=-39.7453 EndY=11.9568 EndZ=0
    g12: ArcOfEllipse CenterX=39.7498 CenterY=5.60031 CenterZ=0 NormalX=0 NormalY=-1e-16 NormalZ=1 MajorRadius=6.35653 MinorRadius=5.50656 AngleXU=-7.28146e-05 StartAngle=4.71245 EndAngle=6.28323
    g13: LineSegment StartX=45.2563 StartY=-31.84 StartZ=0 EndX=45.2563 EndY=5.6003 EndZ=0
    g14: LineSegment StartX=-45.25 StartY=-31.84 StartZ=0 EndX=45.2563 EndY=-31.84 EndZ=0
    g15: LineSegment StartX=-45.25 StartY=5.60814 StartZ=0 EndX=-45.25 EndY=-31.84 EndZ=0
    g16: ArcOfCircle CenterX=-26.25 CenterY=-24.34 CenterZ=0 NormalX=0 NormalY=0 NormalZ=1 AngleXU=0 Radius=4 StartAngle=4.71239 EndAngle=7.85398
    g17: ArcOfCircle CenterX=-33.25 CenterY=-24.34 CenterZ=0 NormalX=0 NormalY=0 NormalZ=1 AngleXU=0 Radius=4 StartAngle=1.5708 EndAngle=4.71239
    g18: LineSegment StartX=-26.25 StartY=-20.34 StartZ=0 EndX=-33.25 EndY=-20.34 EndZ=0
    g19: LineSegment StartX=-33.25 StartY=-28.34 StartZ=0 EndX=-26.25 EndY=-28.34 EndZ=0
  constraints (40):
    c: Vertical(g0)
    c: Coincident(g0,g1)
    c: Vertical(g1)
    c: Coincident(g1,g2)
    c: Horizontal(g2)
    c: Coincident(g2,g3)
    c: Horizontal(g3)
    c: Coincident(g3,g4)
    c: Horizontal(g4)
    c: Coincident(g4,g5)
    c: Vertical(g5)
    c: Coincident(g5,g6)
    c: Vertical(g6)
    c: Coincident(g6,g7)
    c: Coincident(g7,g8)
    c: Horizontal(g8)
    c: Coincident(g8,g9)
    c: Coincident(g9,g0)
    c: Coincident(g10,g11)
    c: Horizontal(g11)
    c: Coincident(g11,g12)
    c: Coincident(g12,g13)
    c: Vertical(g13)
    c: Coincident(g13,g14)
    c: Horizontal(g14)
    c: Coincident(g14,g15)
    c: Vertical(g15)
    c: Coincident(g15,g10)
    c: Tangent(g16,g18) = -1.5708
    c: Tangent(g18,g17) = -1.5708
    c: Tangent(g17,g19) = -1.5708
    c: Tangent(g19,g16) = -1.5708
    c: Equal(g16,g17)
    c: Horizontal(g18)
    c: DistanceX(g18,g18) = 7
    c: Radius(g16) = 4
    c: DistanceY(g14,g-1) = 31.84
    c: DistanceX(g14,g-1) = 45.25
    c: DistanceY(g14,g17) = 3.5
    c: DistanceX(g14,g17) = 12
FEATURE [Sketcher::SketchObject] Sketch013
  ExternalGeometry = -> [Sketch]
  FullyConstrained = true
  Placement = pos=(0,0,4) rot=(0,0,1;0rad)
  sketch-geometry (20):
    g0: ArcOfCircle CenterX=-39.75 CenterY=25.5 CenterZ=0 NormalX=0 NormalY=0 NormalZ=1 AngleXU=0 Radius=7.5 StartAngle=1.5708 EndAngle=3.14159
    g1: LineSegment StartX=-39.75 StartY=33 StartZ=0 EndX=39.75 EndY=33 EndZ=0
    g2: ArcOfCircle CenterX=39.75 CenterY=25.5 CenterZ=0 NormalX=0 NormalY=0 NormalZ=1 AngleXU=0 Radius=7.5 StartAngle=1e-16 EndAngle=1.5708
    g3: LineSegment StartX=47.25 StartY=25.5 StartZ=0 EndX=47.25 EndY=-25.5 EndZ=0
    g4: ArcOfCircle CenterX=39.75 CenterY=-25.5 CenterZ=0 NormalX=0 NormalY=0 NormalZ=1 AngleXU=0 Radius=7.5 StartAngle=4.71239 EndAngle=6.28319
    g5: LineSegment StartX=39.75 StartY=-33 StartZ=0 EndX=-39.75 EndY=-33 EndZ=0
    g6: ArcOfCircle CenterX=-39.75 CenterY=-25.5 CenterZ=0 NormalX=0 NormalY=0 NormalZ=1 AngleXU=0 Radius=7.5 StartAngle=3.14159 EndAngle=4.71239
    g7: LineSegment StartX=-47.25 StartY=-25.5 StartZ=0 EndX=-47.25 EndY=25.5 EndZ=0
    g8: GeomPoint X=-47.25 Y=33 Z=0
    g9: GeomPoint X=47.25 Y=-33 Z=0
    g10: ArcOfCircle CenterX=-39.75 CenterY=25.5 CenterZ=0 NormalX=0 NormalY=0 NormalZ=1 AngleXU=0 Radius=5.3 StartAngle=1.5708 EndAngle=3.14159
    g11: LineSegment StartX=-39.75 StartY=30.8 StartZ=0 EndX=39.75 EndY=30.8 EndZ=0
    g12: ArcOfCircle CenterX=39.75 CenterY=25.5 CenterZ=0 NormalX=0 NormalY=0 NormalZ=1 AngleXU=0 Radius=5.3 StartAngle=1e-16 EndAngle=1.5708
    g13: LineSegment StartX=45.05 StartY=25.5 StartZ=0 EndX=45.05 EndY=-25.5 EndZ=0
    g14: ArcOfCircle CenterX=39.75 CenterY=-25.5 CenterZ=0 NormalX=0 NormalY=0 NormalZ=1 AngleXU=0 Radius=5.3 StartAngle=4.71239 EndAngle=6.28319
    g15: LineSegment StartX=39.75 StartY=-30.8 StartZ=0 EndX=-39.75 EndY=-30.8 EndZ=0
    g16: ArcOfCircle CenterX=-39.75 CenterY=-25.5 CenterZ=0 NormalX=0 NormalY=0 NormalZ=1 AngleXU=0 Radius=5.3 StartAngle=3.14159 EndAngle=4.71239
    g17: LineSegment StartX=-45.05 StartY=-25.5 StartZ=0 EndX=-45.05 EndY=25.5 EndZ=0
    g18: GeomPoint X=-45.05 Y=30.8 Z=0
    g19: GeomPoint X=45.05 Y=-30.8 Z=0
  constraints (45):
    c: Tangent(g0,g1) = 1.5708
    c: Tangent(g1,g2) = 1.5708
    c: Tangent(g2,g3) = 1.5708
    c: Tangent(g3,g4) = 1.5708
    c: Tangent(g4,g5) = 1.5708
    c: Tangent(g5,g6) = 1.5708
    c: Tangent(g6,g7) = 1.5708
    c: Tangent(g7,g0) = 1.5708
    c: Horizontal(g1)
    c: Horizontal(g5)
    c: Vertical(g3)
    c: Vertical(g7)
    c: Equal(g0,g2)
    c: Equal(g2,g4)
    c: Equal(g4,g6)
    c: PointOnObject(g8,g1)
    c: PointOnObject(g8,g7)
    c: PointOnObject(g9,g3)
    c: PointOnObject(g9,g5)
    c: Coincident(g0,g-3)
    c: Horizontal(g-3,g0)
    c: Tangent(g10,g11) = 1.5708
    c: Tangent(g12,g13) = 1.5708
    c: Tangent(g13,g14) = 1.5708
    c: Tangent(g14,g15) = 1.5708
    c: Tangent(g15,g16) = 1.5708
    c: Tangent(g16,g17) = 1.5708
    c: Tangent(g17,g10) = 1.5708
    c: Horizontal(g11)
    c: Horizontal(g15)
    c: Vertical(g13)
    c: Vertical(g17)
    c: Equal(g10,g12)
    c: Equal(g12,g14)
    c: Equal(g14,g16)
    c: PointOnObject(g18,g11)
    c: PointOnObject(g18,g17)
    c: PointOnObject(g19,g13)
    c: PointOnObject(g19,g15)
    c: Coincident(g14,g4)
    c: Coincident(g11,g12)
    c: Coincident(g0,g10)
    c: Vertical(g12,g11)
    c: Coincident(g14,g-4)
    c: DistanceX(g0,g10) = 2.2
FEATURE [Part::Extrusion] Extrude011  label="Extrude_inner"
  Base = -> Sketch013
  Dir = (0,0,1)
  DirMode = 2
  FaceMakerClass = Part::FaceMakerBullseye
  LengthFwd = 52
  LengthRev = 0
  Solid = true
  Symmetric = false
FEATURE [Sketcher::SketchObject] Sketch014
  ExternalGeometry = -> [Sketch013]
  FullyConstrained = true
  sketch-geometry (10):
    g0: ArcOfCircle CenterX=-39.75 CenterY=25.5 CenterZ=0 NormalX=0 NormalY=0 NormalZ=1 AngleXU=0 Radius=5.1 StartAngle=1.5708 EndAngle=3.14159
    g1: LineSegment StartX=-39.75 StartY=30.6 StartZ=0 EndX=39.75 EndY=30.6 EndZ=0
    g2: ArcOfCircle CenterX=39.75 CenterY=25.5 CenterZ=0 NormalX=0 NormalY=0 NormalZ=1 AngleXU=0 Radius=5.1 StartAngle=3e-16 EndAngle=1.5708
    g3: LineSegment StartX=44.85 StartY=25.5 StartZ=0 EndX=44.85 EndY=-25.5 EndZ=0
    g4: ArcOfCircle CenterX=39.75 CenterY=-25.5 CenterZ=0 NormalX=0 NormalY=0 NormalZ=1 AngleXU=0 Radius=5.1 StartAngle=4.71239 EndAngle=6.28319
    g5: LineSegment StartX=39.75 StartY=-30.6 StartZ=0 EndX=-39.75 EndY=-30.6 EndZ=0
    g6: ArcOfCircle CenterX=-39.75 CenterY=-25.5 CenterZ=0 NormalX=0 NormalY=0 NormalZ=1 AngleXU=0 Radius=5.1 StartAngle=3.14159 EndAngle=4.71239
    g7: LineSegment StartX=-44.85 StartY=-25.5 StartZ=0 EndX=-44.85 EndY=25.5 EndZ=0
    g8: GeomPoint X=-44.85 Y=30.6 Z=0
    g9: GeomPoint X=44.85 Y=-30.6 Z=0
  constraints (30):
    c: Horizontal(g1)
    c: Horizontal(g5)
    c: Vertical(g3)
    c: Vertical(g7)
    c: Equal(g0,g2)
    c: Equal(g2,g4)
    c: Equal(g4,g6)
    c: PointOnObject(g8,g1)
    c: PointOnObject(g8,g7)
    c: PointOnObject(g9,g3)
    c: PointOnObject(g9,g5)
    c: Coincident(g4,g-4)
    c: Coincident(g0,g-3)
    c: DistanceX(g-3,g0) = 0.2
    c: Coincident(g1,g0)
    c: Vertical(g0,g0)
    c: Coincident(g0,g7)
    c: Horizontal(g-3,g0)
    c: Coincident(g7,g6)
    c: Coincident(g5,g6)
    c: Horizontal(g6,g6)
    c: Vertical(g6,g5)
    c: Coincident(g3,g4)
    c: Coincident(g4,g5)
    c: Horizontal(g3,g-4)
    c: Vertical(g4,g-4)
    c: Coincident(g2,g3)
    c: Coincident(g1,g2)
    c: Vertical(g1,g2)
    c: Horizontal(g2,g2)
FEATURE [Part::Extrusion] Extrude012
  Base = -> Sketch014
  Dir = (0,0,1)
  DirMode = 2
  FaceMakerClass = Part::FaceMakerBullseye
  LengthFwd = 52
  LengthRev = 0
  Solid = true
  Symmetric = false
FEATURE [Part::Cut] Cut004
  Base = -> Extrude012
  Tool = -> Box001
FEATURE [Part::Box] Box008  label="Cube008"
  AttacherType = Attacher::AttachEngine3D
  Height = 100
  Length = 100
  Placement = pos=(-50,36.8,-0.6) rot=(1,0,0;0.523599rad)
  Width = 100
FEATURE [Part::Cut] Cut005
  Base = -> Cut004
  Tool = -> Box008
FEATURE [Part::FeaturePython] Facebinder  label="inner_bottom"  # WARN: FeaturePython — macro-defined, semantics opaque (R4)
  Area = 4267.09
  Extrusion = 0
  Faces = -> [Cut005]
  RemoveSplitter = false
  Sew = false
FEATURE [Part::FeaturePython] Facebinder001  label="inner_back"  # WARN: FeaturePython — macro-defined, semantics opaque (R4)
  Area = 3849.5
  Extrusion = 0
  Faces = -> [Cut005]
  RemoveSplitter = false
  Sew = false
FEATURE [Part::Extrusion] Extrude013
  Base = -> Facebinder
  Dir = (0,0.866025,0.5)
  DirMode = 2
  FaceMakerClass = Part::FaceMakerBullseye
  LengthFwd = 2
  LengthRev = 0
  Reversed = true
  Solid = false
  Symmetric = false
FEATURE [Part::Extrusion] Extrude014
  Base = -> Facebinder001
  Dir = (0,-0.5,0.866025)
  DirMode = 2
  FaceMakerClass = Part::FaceMakerBullseye
  LengthFwd = 1
  LengthRev = 0
  Reversed = true
  Solid = false
  Symmetric = false
FEATURE [Part::FeaturePython] Facebinder002  # WARN: FeaturePython — macro-defined, semantics opaque (R4)
  Area = 569.521
  Extrusion = 0
  Faces = -> [Connect]
  RemoveSplitter = false
  Sew = false
FEATURE [Sketcher::SketchObject] Sketch015
  FullyConstrained = false
  Placement = pos=(0,-20.65,35.7668) rot=(1,0,0;0.523599rad)
  sketch-geometry (16):
    g0: LineSegment StartX=-47.25 StartY=-5.6003 StartZ=0 EndX=-47.25 EndY=31.841 EndZ=0
    g1: ArcOfEllipse CenterX=-39.75 CenterY=-5.6003 CenterZ=0 NormalX=0 NormalY=-3e-16 NormalZ=1 MajorRadius=8.66025 MinorRadius=7.5 AngleXU=-3.14159 StartAngle=4.71239 EndAngle=6.28319
    g2: LineSegment StartX=39.75 StartY=-14.2606 StartZ=0 EndX=-39.75 EndY=-14.2606 EndZ=0
    g3: ArcOfEllipse CenterX=39.75 CenterY=-5.6003 CenterZ=0 NormalX=0 NormalY=-3e-16 NormalZ=1 MajorRadius=8.66025 MinorRadius=7.5 AngleXU=-3.14159 StartAngle=0 EndAngle=1.5708
    g4: LineSegment StartX=47.25 StartY=31.841 StartZ=0 EndX=47.25 EndY=-5.6003 EndZ=0
    g5: LineSegment StartX=47.25 StartY=33.841 StartZ=0 EndX=47.25 EndY=31.841 EndZ=0
    g6: LineSegment StartX=45.25 StartY=33.841 StartZ=0 EndX=47.25 EndY=33.841 EndZ=0
    g7: LineSegment StartX=-45.25 StartY=33.841 StartZ=0 EndX=45.25 EndY=33.841 EndZ=0
    g8: LineSegment StartX=-47.25 StartY=33.841 StartZ=0 EndX=-45.25 EndY=33.841 EndZ=0
    g9: LineSegment StartX=-47.25 StartY=31.841 StartZ=0 EndX=-47.25 EndY=33.841 EndZ=0
    g10: ArcOfEllipse CenterX=-39.75 CenterY=-5.6003 CenterZ=0 NormalX=0 NormalY=-3e-16 NormalZ=1 MajorRadius=6.35085 MinorRadius=5.5 AngleXU=-3.14159 StartAngle=4.71239 EndAngle=6.28319
    g11: LineSegment StartX=-45.25 StartY=-5.6003 StartZ=0 EndX=-45.25 EndY=31.841 EndZ=0
    g12: LineSegment StartX=-45.25 StartY=31.841 StartZ=0 EndX=45.25 EndY=31.841 EndZ=0
    g13: LineSegment StartX=45.25 StartY=31.841 StartZ=0 EndX=45.25 EndY=-5.6003 EndZ=0
    g14: ArcOfEllipse CenterX=39.75 CenterY=-5.6003 CenterZ=0 NormalX=0 NormalY=-3e-16 NormalZ=1 MajorRadius=6.35085 MinorRadius=5.5 AngleXU=-3.14159 StartAngle=0 EndAngle=1.5708
    g15: LineSegment StartX=39.75 StartY=-11.9512 StartZ=0 EndX=-39.75 EndY=-11.9512 EndZ=0
  constraints (28):
    c: Vertical(g0)
    c: Coincident(g0,g1)
    c: Coincident(g1,g2)
    c: Horizontal(g2)
    c: Coincident(g2,g3)
    c: Coincident(g3,g4)
    c: Vertical(g4)
    c: Coincident(g4,g5)
    c: Vertical(g5)
    c: Coincident(g5,g6)
    c: Horizontal(g6)
    c: Coincident(g6,g7)
    c: Horizontal(g7)
    c: Coincident(g7,g8)
    c: Horizontal(g8)
    c: Coincident(g8,g9)
    c: Vertical(g9)
    c: Coincident(g9,g0)
    c: Coincident(g10,g11)
    c: Vertical(g11)
    c: Coincident(g11,g12)
    c: Horizontal(g12)
    c: Coincident(g12,g13)
    c: Vertical(g13)
    c: Coincident(g13,g14)
    c: Coincident(g14,g15)
    c: Horizontal(g15)
    c: Coincident(g15,g10)
FEATURE [Part::Extrusion] Extrude015
  Base = -> Sketch015
  Dir = (0,-0.5,0.866025)
  DirMode = 2
  FaceMakerClass = Part::FaceMakerBullseye
  LengthFwd = 1
  LengthRev = 0
  Solid = true
  Symmetric = false
FEATURE [Part::FeaturePython] Connect003  label="inner_complete"  # WARN: FeaturePython — macro-defined, semantics opaque (R4)
  Objects = -> [Extrude013,Extrude014,Extrude015]
  Tolerance = 0
FEATURE [Sketcher::SketchObject] Sketch016
  ExternalGeometry = -> [Connect003]
  FullyConstrained = true
  Placement = pos=(0,0,0) rot=(0.57735,0.57735,0.57735;2.0944rad)
  sketch-geometry (3):
    g0: LineSegment StartX=5.45814 StartY=49.6857 StartZ=0 EndX=-16.1925 EndY=37.1857 EndZ=0
    g1: LineSegment StartX=5.45814 StartY=49.6857 StartZ=0 EndX=17.9581 EndY=28.0351 EndZ=0
    g2: ArcOfCircle CenterX=5.45814 CenterY=49.6857 CenterZ=0 NormalX=0 NormalY=0 NormalZ=1 AngleXU=0 Radius=25 StartAngle=3.66519 EndAngle=5.23599
  constraints (8):
    c: Coincident(g0,g-4)
    c: PointOnObject(g0,g-4)
    c: Coincident(g1,g0)
    c: PointOnObject(g1,g-3)
    c: Coincident(g2,g0)
    c: Coincident(g2,g0)
    c: Coincident(g2,g1)
    c: Distance(g0) = 25
FEATURE [Part::Extrusion] Extrude016
  Base = -> Sketch016
  Dir = (1,0,0)
  DirMode = 2
  FaceMakerClass = Part::FaceMakerBullseye
  LengthFwd = 1.2
  LengthRev = 0
  Placement = pos=(43.6,0,0) rot=(0,0,1;0rad)
  Solid = true
  Symmetric = false
FEATURE [Part::Extrusion] Extrude017
  Base = -> Sketch016
  Dir = (1,0,0)
  DirMode = 2
  FaceMakerClass = Part::FaceMakerBullseye
  LengthFwd = 1.2
  LengthRev = 0
  Placement = pos=(-44.7,0,0) rot=(0,0,1;0rad)
  Solid = true
  Symmetric = false
FEATURE [Sketcher::SketchObject] Sketch017
  ExternalGeometry = -> [Connect003,Extrude017,Extrude016]
  FullyConstrained = true
  MapMode = 5
  Placement = pos=(0,25.6081,14.7849) rot=(1,0,0;2.0944rad)
  Support = -> [Connect003]
  sketch-geometry (16):
    g0: LineSegment StartX=-43.5 StartY=40.3 StartZ=0 EndX=43.6 EndY=40.3 EndZ=0
    g1: LineSegment StartX=43.6 StartY=40.3 StartZ=0 EndX=43.6 EndY=20.3 EndZ=0
    g2: LineSegment StartX=-43.5 StartY=20.3 StartZ=0 EndX=-43.5 EndY=40.3 EndZ=0
    g3: LineSegment StartX=-40 StartY=20.3 StartZ=0 EndX=-43.5 EndY=20.3 EndZ=0
    g4: LineSegment StartX=-40 StartY=37.8 StartZ=0 EndX=-40 EndY=20.3 EndZ=0
    g5: LineSegment StartX=-29 StartY=37.8 StartZ=0 EndX=-40 EndY=37.8 EndZ=0
    g6: LineSegment StartX=-29 StartY=20.3 StartZ=0 EndX=-29 EndY=37.8 EndZ=0
    g7: LineSegment StartX=-20.5 StartY=20.3 StartZ=0 EndX=-29 EndY=20.3 EndZ=0
    g8: LineSegment StartX=-20.5 StartY=37.8 StartZ=0 EndX=-20.5 EndY=20.3 EndZ=0
    g9: LineSegment StartX=43.6 StartY=20.3 StartZ=0 EndX=23.5 EndY=20.3 EndZ=0
    g10: LineSegment StartX=23.5 StartY=20.3 StartZ=0 EndX=23.5 EndY=37.8 EndZ=0
    g11: LineSegment StartX=4 StartY=37.8 StartZ=0 EndX=-20.5 EndY=37.8 EndZ=0
    g12: LineSegment StartX=4 StartY=20.3 StartZ=0 EndX=4 EndY=37.8 EndZ=0
    g13: LineSegment StartX=11.5 StartY=20.3 StartZ=0 EndX=4 EndY=20.3 EndZ=0
    g14: LineSegment StartX=23.5 StartY=37.8 StartZ=0 EndX=11.5 EndY=37.8 EndZ=0
    g15: LineSegment StartX=11.5 StartY=37.8 StartZ=0 EndX=11.5 EndY=20.3 EndZ=0
  constraints (48):
    c: Coincident(g0,g1)
    c: Coincident(g1,g9)
    c: Coincident(g2,g0)
    c: Vertical(g1)
    c: Vertical(g2)
    c: PointOnObject(g0,g-3)
    c: PointOnObject(g0,g-5)
    c: PointOnObject(g0,g-4)
    c: Coincident(g4,g3)
    c: Coincident(g5,g4)
    c: Horizontal(g3)
    c: Vertical(g4)
    c: Coincident(g6,g5)
    c: Horizontal(g5)
    c: Coincident(g7,g6)
    c: Horizontal(g7)
    c: Coincident(g11,g8)
    c: Vertical(g6)
    c: Vertical(g8)
    c: DistanceX(g3,g3) = 3.5
    c: DistanceY(g4,g0) = 2.5
    c: Horizontal(g5,g11)
    c: Horizontal(g3,g6)
    c: Coincident(g8,g7)
    c: DistanceX(g7,g7) = 8.5
    c: DistanceX(g5,g5) = 11
    c: Coincident(g3,g2)
    c: DistanceY(g2,g2) = 20
    c: Coincident(g10,g14)
    c: Coincident(g9,g10)
    c: Horizontal(g9)
    c: Vertical(g10)
    c: Horizontal(g7,g9)
    c: Coincident(g12,g11)
    c: Horizontal(g11)
    c: Coincident(g13,g12)
    c: Coincident(g15,g13)
    c: Horizontal(g13)
    c: Coincident(g14,g15)
    c: Horizontal(g14)
    c: Vertical(g15)
    c: Vertical(g12)
    c: DistanceX(g13,g13) = 7.5
    c: Horizontal(g7,g12)
    c: Horizontal(g11,g14)
    c: PointOnObject(g0,g-3)
    c: DistanceX(g11,g11) = 24.5
    c: DistanceX(g14,g14) = 12
FEATURE [Part::Extrusion] Extrude018
  Base = -> Sketch017
  Dir = (0,-0.866025,-0.5)
  DirMode = 2
  FaceMakerClass = Part::FaceMakerBullseye
  LengthFwd = 2.5
  LengthRev = 0
  Solid = true
  Symmetric = false
FEATURE [Sketcher::SketchObject] Sketch018
  AttachmentOffset = pos=(0,0,2.5) rot=(0,0,1;0rad)
  ExternalGeometry = -> [Sketch017]
  FullyConstrained = true
  MapMode = 2
  Placement = pos=(0,23.4431,13.5349) rot=(1,0,0;2.0944rad)
  Support = -> [Sketch017]
  sketch-geometry (13):
    g0: LineSegment StartX=43.6 StartY=40.3 StartZ=0 EndX=43.6 EndY=20.3 EndZ=0
    g1: LineSegment StartX=26 StartY=20.3 StartZ=0 EndX=26 EndY=40.3 EndZ=0
    g2: LineSegment StartX=26 StartY=40.3 StartZ=0 EndX=43.6 EndY=40.3 EndZ=0
    g3: LineSegment StartX=-25.5 StartY=40.3 StartZ=0 EndX=-23 EndY=40.3 EndZ=0
    g4: LineSegment StartX=-25.5 StartY=40.3 StartZ=0 EndX=-25.5 EndY=20.3 EndZ=0
    g5: LineSegment StartX=-23 StartY=40.3 StartZ=0 EndX=-23 EndY=20.3 EndZ=0
    g6: LineSegment StartX=-25.5 StartY=20.3 StartZ=0 EndX=-23 EndY=20.3 EndZ=0
    g7: LineSegment StartX=-25.5 StartY=20.3 StartZ=0 EndX=-23 EndY=20.3 EndZ=0
    g8: LineSegment StartX=9 StartY=20.3 StartZ=0 EndX=6.5 EndY=20.3 EndZ=0
    g9: LineSegment StartX=6.5 StartY=20.3 StartZ=0 EndX=6.5 EndY=40.3 EndZ=0
    g10: LineSegment StartX=6.5 StartY=40.3 StartZ=0 EndX=9 EndY=40.3 EndZ=0
    g11: LineSegment StartX=9 StartY=40.3 StartZ=0 EndX=9 EndY=20.3 EndZ=0
    g12: LineSegment StartX=43.6 StartY=20.3 StartZ=0 EndX=26 EndY=20.3 EndZ=0
  constraints (36):
    c: Coincident(g0,g-5)
    c: Vertical(g1)
    c: Coincident(g2,g1)
    c: Coincident(g2,g0)
    c: PointOnObject(g3,g-3)
    c: PointOnObject(g3,g-3)
    c: Coincident(g4,g3)
    c: PointOnObject(g4,g-4)
    c: Vertical(g4)
    c: Coincident(g5,g3)
    c: PointOnObject(g5,g-4)
    c: Vertical(g5)
    c: Coincident(g6,g4)
    c: Coincident(g6,g5)
    c: Coincident(g7,g4)
    c: Coincident(g7,g5)
    c: Coincident(g8,g9)
    c: Coincident(g9,g10)
    c: Coincident(g10,g11)
    c: Horizontal(g10)
    c: Vertical(g9)
    c: PointOnObject(g9,g-3)
    c: Equal(g7,g8)
    c: DistanceX(g5,g-4) = 2.5
    c: Coincident(g8,g11)
    c: Vertical(g11)
    c: DistanceX(g7,g7) = 2.5
    c: Horizontal(g8)
    c: Horizontal(g8,g-6)
    c: DistanceX(g-6,g8) = 2.5
    c: Coincident(g12,g0)
    c: Coincident(g12,g1)
    c: DistanceX(g-5,g1) = 2.5
    c: PointOnObject(g1,g-5)
    c: PointOnObject(g1,g-3)
    c: Coincident(g0,g-3)
FEATURE [Part::Extrusion] Extrude019
  Base = -> Sketch018
  Dir = (0,-0.866025,-0.5)
  DirMode = 2
  FaceMakerClass = Part::FaceMakerBullseye
  LengthFwd = 2
  LengthRev = 0
  Solid = true
  Symmetric = false
FEATURE [Sketcher::SketchObject] Sketch019
  AttachmentOffset = pos=(0,0,4.5) rot=(0,0,1;0rad)
  ExternalGeometry = -> [Sketch017]
  FullyConstrained = true
  MapMode = 2
  Placement = pos=(0,21.711,12.5349) rot=(1,0,0;2.0944rad)
  Support = -> [Sketch017]
  sketch-geometry (16):
    g0: LineSegment StartX=-43.5 StartY=40.3 StartZ=0 EndX=-40 EndY=40.3 EndZ=0
    g1: LineSegment StartX=-40 StartY=40.3 StartZ=0 EndX=-40 EndY=20.3 EndZ=0
    g2: LineSegment StartX=-40 StartY=20.3 StartZ=0 EndX=-43.5 EndY=20.3 EndZ=0
    g3: LineSegment StartX=-43.5 StartY=20.3 StartZ=0 EndX=-43.5 EndY=40.3 EndZ=0
    g4: LineSegment StartX=-29 StartY=40.3 StartZ=0 EndX=-20.5 EndY=40.3 EndZ=0
    g5: LineSegment StartX=-20.5 StartY=40.3 StartZ=0 EndX=-20.5 EndY=20.3 EndZ=0
    g6: LineSegment StartX=-20.5 StartY=20.3 StartZ=0 EndX=-29 EndY=20.3 EndZ=0
    g7: LineSegment StartX=-29 StartY=20.3 StartZ=0 EndX=-29 EndY=40.3 EndZ=0
    g8: LineSegment StartX=4 StartY=40.3 StartZ=0 EndX=11.5 EndY=40.3 EndZ=0
    g9: LineSegment StartX=11.5 StartY=40.3 StartZ=0 EndX=11.5 EndY=20.3 EndZ=0
    g10: LineSegment StartX=11.5 StartY=20.3 StartZ=0 EndX=4 EndY=20.3 EndZ=0
    g11: LineSegment StartX=4 StartY=20.3 StartZ=0 EndX=4 EndY=40.3 EndZ=0
    g12: LineSegment StartX=23.5 StartY=40.3 StartZ=0 EndX=43.6 EndY=40.3 EndZ=0
    g13: LineSegment StartX=43.6 StartY=40.3 StartZ=0 EndX=43.6 EndY=20.3 EndZ=0
    g14: LineSegment StartX=43.6 StartY=20.3 StartZ=0 EndX=23.5 EndY=20.3 EndZ=0
    g15: LineSegment StartX=23.5 StartY=20.3 StartZ=0 EndX=23.5 EndY=40.3 EndZ=0
  constraints (40):
    c: Coincident(g0,g1)
    c: Coincident(g1,g2)
    c: Coincident(g2,g3)
    c: Coincident(g3,g0)
    c: Horizontal(g0)
    c: Horizontal(g2)
    c: Vertical(g1)
    c: Vertical(g3)
    c: Coincident(g0,g-3)
    c: Coincident(g1,g-4)
    c: Coincident(g4,g5)
    c: Coincident(g5,g6)
    c: Coincident(g6,g7)
    c: Coincident(g7,g4)
    c: Horizontal(g4)
    c: Vertical(g5)
    c: Vertical(g7)
    c: Horizontal(g4,g0)
    c: Coincident(g6,g-5)
    c: Coincident(g-5,g5)
    c: Coincident(g8,g9)
    c: Coincident(g9,g10)
    c: Coincident(g10,g11)
    c: Coincident(g11,g8)
    c: Horizontal(g8)
    c: Vertical(g9)
    c: Vertical(g11)
    c: Horizontal(g0,g8)
    c: Coincident(g10,g-6)
    c: Coincident(g9,g-6)
    c: Coincident(g12,g13)
    c: Coincident(g13,g14)
    c: Coincident(g14,g15)
    c: Coincident(g15,g12)
    c: Horizontal(g12)
    c: Vertical(g13)
    c: Vertical(g15)
    c: Coincident(g14,g-7)
    c: Coincident(g13,g-7)
    c: Horizontal(g0,g12)
FEATURE [Part::Extrusion] Extrude020
  Base = -> Sketch019
  Dir = (0,-0.866025,-0.5)
  DirMode = 2
  FaceMakerClass = Part::FaceMakerBullseye
  LengthFwd = 2
  LengthRev = 0
  Solid = true
  Symmetric = false
FEATURE [Sketcher::SketchObject] Sketch020
  ExternalGeometry = -> [Extrude020,Extrude018]
  FullyConstrained = true
  MapMode = 5
  Placement = pos=(0,-21.15,36.6329) rot=(1,0,0;0.523599rad)
  Support = -> [Connect003]
  sketch-geometry (26):
    g0: ArcOfCircle CenterX=-37 CenterY=24.6697 CenterZ=0 NormalX=0 NormalY=0 NormalZ=1 AngleXU=0 Radius=2 StartAngle=1.5708 EndAngle=4.71239
    g1: ArcOfCircle CenterX=-32 CenterY=24.6697 CenterZ=0 NormalX=0 NormalY=0 NormalZ=1 AngleXU=0 Radius=2 StartAngle=4.71239 EndAngle=7.85398
    g2: LineSegment StartX=-37 StartY=22.6697 StartZ=0 EndX=-32 EndY=22.6697 EndZ=0
    g3: LineSegment StartX=-32 StartY=26.6697 StartZ=0 EndX=-37 EndY=26.6697 EndZ=0
    g4: ArcOfCircle CenterX=-17.5 CenterY=24.6697 CenterZ=0 NormalX=0 NormalY=0 NormalZ=1 AngleXU=0 Radius=2 StartAngle=1.5708 EndAngle=4.71239
    g5: ArcOfCircle CenterX=1 CenterY=24.6697 CenterZ=0 NormalX=0 NormalY=0 NormalZ=1 AngleXU=0 Radius=2 StartAngle=4.71239 EndAngle=7.85398
    g6: LineSegment StartX=-17.5 StartY=22.6697 StartZ=0 EndX=1 EndY=22.6697 EndZ=0
    g7: LineSegment StartX=1 StartY=26.6697 StartZ=0 EndX=-17.5 EndY=26.6697 EndZ=0
    g8: LineSegment StartX=-40 StartY=25.0697 StartZ=0 EndX=-37 EndY=24.6697 EndZ=0
    g9: LineSegment StartX=-29 StartY=25.0697 StartZ=0 EndX=-32 EndY=24.6697 EndZ=0
    g10: LineSegment StartX=-20.5 StartY=25.0697 StartZ=0 EndX=-17.5 EndY=24.6697 EndZ=0
    g11: LineSegment StartX=1 StartY=24.6697 StartZ=0 EndX=4 EndY=25.0697 EndZ=0
    g12: ArcOfCircle CenterX=14.5 CenterY=24.6697 CenterZ=0 NormalX=0 NormalY=0 NormalZ=1 AngleXU=0 Radius=2 StartAngle=1.5708 EndAngle=4.71239
    g13: ArcOfCircle CenterX=20.5 CenterY=24.6697 CenterZ=0 NormalX=0 NormalY=0 NormalZ=1 AngleXU=0 Radius=2 StartAngle=4.71239 EndAngle=7.85398
    g14: LineSegment StartX=14.5 StartY=22.6697 StartZ=0 EndX=20.5 EndY=22.6697 EndZ=0
    g15: LineSegment StartX=20.5 StartY=26.6697 StartZ=0 EndX=14.5 EndY=26.6697 EndZ=0
    g16: LineSegment StartX=11.5 StartY=25.0697 StartZ=0 EndX=14.5 EndY=24.6697 EndZ=0
    g17: LineSegment StartX=20.5 StartY=24.6697 StartZ=0 EndX=23.5 EndY=25.0697 EndZ=0
    g18: LineSegment StartX=28.5 StartY=29.5697 StartZ=0 EndX=33.5 EndY=29.5697 EndZ=0
    g19: LineSegment StartX=33.5 StartY=29.5697 StartZ=0 EndX=33.5 EndY=24.5697 EndZ=0
    g20: LineSegment StartX=33.5 StartY=24.5697 StartZ=0 EndX=28.5 EndY=24.5697 EndZ=0
    g21: LineSegment StartX=28.5 StartY=24.5697 StartZ=0 EndX=28.5 EndY=29.5697 EndZ=0
    g22: LineSegment StartX=36 StartY=29.5697 StartZ=0 EndX=41 EndY=29.5697 EndZ=0
    g23: LineSegment StartX=41 StartY=29.5697 StartZ=0 EndX=41 EndY=24.5697 EndZ=0
    g24: LineSegment StartX=41 StartY=24.5697 StartZ=0 EndX=36 EndY=24.5697 EndZ=0
    g25: LineSegment StartX=36 StartY=24.5697 StartZ=0 EndX=36 EndY=29.5697 EndZ=0
  constraints (66):
    c: Tangent(g0,g2) = -1.5708
    c: Tangent(g2,g1) = -1.5708
    c: Tangent(g1,g3) = -1.5708
    c: Tangent(g3,g0) = -1.5708
    c: Equal(g0,g1)
    c: Horizontal(g2)
    c: DistanceY(g1,g1) = 4
    c: DistanceX(g3,g3) = 5
    c: DistanceY(g0,g-4) = 0.4
    c: Tangent(g4,g6) = -1.5708
    c: Tangent(g6,g5) = -1.5708
    c: Tangent(g5,g7) = -1.5708
    c: Tangent(g7,g4) = -1.5708
    c: Equal(g4,g5)
    c: Horizontal(g6)
    c: Equal(g4,g1)
    c: Horizontal(g1,g4)
    c: Coincident(g8,g-3)
    c: Coincident(g8,g0)
    c: Coincident(g9,g-5)
    c: Coincident(g9,g1)
    c: Equal(g9,g8)
    c: Coincident(g10,g-6)
    c: Coincident(g10,g4)
    c: Coincident(g11,g5)
    c: Coincident(g11,g-7)
    c: Equal(g10,g11)
    c: Equal(g9,g10)
    c: Tangent(g12,g14) = -1.5708
    c: Tangent(g14,g13) = -1.5708
    c: Tangent(g13,g15) = -1.5708
    c: Tangent(g15,g12) = -1.5708
    c: Equal(g12,g13)
    c: Horizontal(g14)
    c: Equal(g5,g12)
    c: Horizontal(g5,g12)
    c: Coincident(g16,g-8)
    c: Coincident(g16,g12)
    c: Coincident(g17,g13)
    c: Coincident(g17,g-9)
    c: Equal(g11,g16)
    c: Equal(g16,g17)
    c: Coincident(g18,g19)
    c: Coincident(g19,g20)
    c: Coincident(g20,g21)
    c: Coincident(g21,g18)
    c: Horizontal(g18)
    c: Horizontal(g20)
    c: Vertical(g19)
    c: Vertical(g21)
    c: Coincident(g22,g23)
    c: Coincident(g23,g24)
    c: Coincident(g24,g25)
    c: Coincident(g25,g22)
    c: Horizontal(g22)
    c: Horizontal(g24)
    c: Vertical(g23)
    c: Vertical(g25)
    c: PointOnObject(g18,g-10)
    c: PointOnObject(g22,g-10)
    c: Equal(g24,g20)
    c: DistanceX(g-11,g20) = 5
    c: DistanceX(g19,g24) = 2.5
    c: DistanceX(g20,g20) = 5
    c: DistanceY(g21,g21) = 5
    c: Horizontal(g19,g24)
FEATURE [Part::Extrusion] Extrude021
  Base = -> Sketch020
  Dir = (0,-0.5,0.866025)
  DirMode = 2
  FaceMakerClass = Part::FaceMakerBullseye
  LengthFwd = 25
  LengthRev = 0
  Reversed = true
  Solid = true
  Symmetric = false
FEATURE [Part::FeaturePython] Connect004  # WARN: FeaturePython — macro-defined, semantics opaque (R4)
  Objects = -> [Extrude020,Extrude019,Extrude018,Extrude017,Extrude016,Connect003]
  Tolerance = 0
FEATURE [Part::Cut] Cut006  label="INNER_COMPLETE"
  Base = -> Connect004
  Tool = -> Extrude021
FEATURE [Mesh::Feature] Mesh004  label="INNER_COMPLETE (Meshed)"
FEATURE [Sketcher::SketchObject] Sketch021
  ExternalGeometry = -> [Cut006,Chamfer002]
  FullyConstrained = true
  MapMode = 5
  Placement = pos=(0,25.6081,14.7849) rot=(1,0,0;2.0944rad)
  Support = -> [Cut006]
  sketch-geometry (10):
    g0: LineSegment StartX=29 StartY=44.3 StartZ=0 EndX=33 EndY=44.3 EndZ=0
    g1: LineSegment StartX=33 StartY=44.3 StartZ=0 EndX=33 EndY=18.3 EndZ=0
    g2: LineSegment StartX=33 StartY=18.3 StartZ=0 EndX=29 EndY=18.3 EndZ=0
    g3: LineSegment StartX=29 StartY=18.3 StartZ=0 EndX=29 EndY=44.3 EndZ=0
    g4: LineSegment StartX=29 StartY=18.3 StartZ=0 EndX=26.5 EndY=12.3 EndZ=0
    g5: LineSegment StartX=33 StartY=18.3 StartZ=0 EndX=30.5 EndY=12.3 EndZ=0
    g6: LineSegment StartX=26.5 StartY=12.3 StartZ=0 EndX=30.5 EndY=12.3 EndZ=0
    g7: LineSegment StartX=30.5 StartY=12.3 StartZ=0 EndX=30.5 EndY=6.3 EndZ=0
    g8: LineSegment StartX=30.5 StartY=6.3 StartZ=0 EndX=26.5 EndY=6.3 EndZ=0
    g9: LineSegment StartX=26.5 StartY=6.3 StartZ=0 EndX=26.5 EndY=12.3 EndZ=0
  constraints (29):
    c: Coincident(g0,g1)
    c: Coincident(g1,g2)
    c: Coincident(g2,g3)
    c: Coincident(g3,g0)
    c: Horizontal(g0)
    c: Horizontal(g2)
    c: Vertical(g1)
    c: Vertical(g3)
    c: DistanceX(g0,g0) = 4
    c: DistanceX(g-3,g-4) = 5
    c: DistanceY(g1,g1) = 26
    c: DistanceY(g-3,g0) = 2
    c: DistanceX(g-3,g0) = 0.5
    c: Coincident(g4,g3)
    c: Coincident(g5,g1)
    c: Parallel(g4,g5)
    c: DistanceX(g5,g1) = 2.5
    c: DistanceY(g5,g1) = 6
    c: Horizontal(g4,g5)
    c: Coincident(g6,g7)
    c: Coincident(g7,g8)
    c: Coincident(g8,g9)
    c: Coincident(g9,g6)
    c: Horizontal(g8)
    c: Vertical(g7)
    c: Vertical(g9)
    c: Coincident(g6,g4)
    c: Coincident(g5,g6)
    c: DistanceY(g9,g9) = 6
FEATURE [Part::Extrusion] Extrude022
  Base = -> Sketch021
  Dir = (0,-0.866025,-0.5)
  DirMode = 2
  FaceMakerClass = Part::FaceMakerBullseye
  LengthFwd = 4
  LengthRev = 0
  Solid = true
  Symmetric = false
FEATURE [Sketcher::SketchObject] Sketch022
  ExternalGeometry = -> [Extrude022,Chamfer002]
  FullyConstrained = true
  MapMode = 5
  Placement = pos=(26.5,0,0) rot=(0.57735,-0.57735,-0.57735;2.0944rad)
  Support = -> [Extrude022]
  sketch-geometry (4):
    g0: LineSegment StartX=-15.994 StartY=23.437 StartZ=0 EndX=-11 EndY=10 EndZ=0
    g1: LineSegment StartX=-19 StartY=10 StartZ=0 EndX=-11 EndY=10 EndZ=0
    g2: LineSegment StartX=-22.4581 StartY=20.2408 StartZ=0 EndX=-19 EndY=10 EndZ=0
    g3: LineSegment StartX=-22.4581 StartY=20.2408 StartZ=0 EndX=-15.994 EndY=23.437 EndZ=0
  constraints (10):
    c: PointOnObject(g1,g-4)
    c: Coincident(g0,g-3)
    c: PointOnObject(g0,g-4)
    c: Coincident(g1,g0)
    c: Coincident(g2,g-5)
    c: Coincident(g2,g1)
    c: DistanceX(g1,g1) = 8
    c: DistanceX(g0,g-4) = 1
    c: Coincident(g3,g2)
    c: Coincident(g3,g0)
FEATURE [Part::Extrusion] Extrude023
  Base = -> Sketch022
  Dir = (-1,0,0)
  DirMode = 2
  FaceMakerClass = Part::FaceMakerBullseye
  LengthFwd = 4
  LengthRev = 0
  Reversed = true
  Solid = true
  Symmetric = false
FEATURE [Part::FeaturePython] Connect005  label="Pin_Boot"  # WARN: FeaturePython — macro-defined, semantics opaque (R4)
  Objects = -> [Extrude022,Extrude023]
  Tolerance = 0
FEATURE [Sketcher::SketchObject] Sketch023
  ExternalGeometry = -> [Cut006,Sketch021]
  FullyConstrained = true
  MapMode = 2
  Placement = pos=(0,25.6081,14.7849) rot=(1,0,0;2.0944rad)
  Support = -> [Sketch021]
  sketch-geometry (9):
    g0: LineSegment StartX=32.5 StartY=10.3 StartZ=0 EndX=36.5 EndY=10.3 EndZ=0
    g1: LineSegment StartX=36.5 StartY=10.3 StartZ=0 EndX=36.5 EndY=6.3 EndZ=0
    g2: LineSegment StartX=36.5 StartY=6.3 StartZ=0 EndX=32.5 EndY=6.3 EndZ=0
    g3: LineSegment StartX=32.5 StartY=6.3 StartZ=0 EndX=32.5 EndY=10.3 EndZ=0
    g4: LineSegment StartX=36.5 StartY=44.3 StartZ=0 EndX=40.5 EndY=44.3 EndZ=0
    g5: LineSegment StartX=40.5 StartY=44.3 StartZ=0 EndX=40.5 EndY=6.3 EndZ=0
    g6: LineSegment StartX=40.5 StartY=6.3 StartZ=0 EndX=36.5 EndY=6.3 EndZ=0
    g7: LineSegment StartX=36.5 StartY=6.3 StartZ=0 EndX=36.5 EndY=10.3 EndZ=0
    g8: LineSegment StartX=36.5 StartY=10.3 StartZ=0 EndX=36.5 EndY=44.3 EndZ=0
  constraints (25):
    c: Coincident(g0,g1)
    c: Coincident(g1,g2)
    c: Coincident(g2,g3)
    c: Coincident(g3,g0)
    c: Horizontal(g0)
    c: Horizontal(g2)
    c: Vertical(g1)
    c: Vertical(g3)
    c: Equal(g3,g2)
    c: Equal(g2,g-6)
    c: DistanceX(g-6,g2) = 2
    c: Horizontal(g-6,g2)
    c: Coincident(g4,g5)
    c: Coincident(g5,g6)
    c: Coincident(g6,g7)
    c: Coincident(g8,g4)
    c: Horizontal(g4)
    c: Horizontal(g6)
    c: Vertical(g5)
    c: Equal(g-5,g4)
    c: Horizontal(g-5,g4)
    c: DistanceX(g-4,g4) = 0.5
    c: Coincident(g7,g8)
    c: Coincident(g0,g7)
    c: Coincident(g1,g6)
FEATURE [Part::Extrusion] Extrude024
  Base = -> Sketch023
  Dir = (0,-0.866025,-0.5)
  DirMode = 2
  FaceMakerClass = Part::FaceMakerBullseye
  LengthFwd = 4
  LengthRev = 0
  Solid = true
  Symmetric = false
FEATURE [Sketcher::SketchObject] Sketch024
  ExternalGeometry = -> [Sketch023,Sketch022,Extrude024]
  FullyConstrained = true
  MapMode = 5
  Placement = pos=(32.5,0,0) rot=(0.57735,-0.57735,-0.57735;2.0944rad)
  Support = -> [Extrude024]
  sketch-geometry (4):
    g0: LineSegment StartX=-19 StartY=10 StartZ=0 EndX=-22.4581 EndY=20.2408 EndZ=0
    g1: LineSegment StartX=-11 StartY=10 StartZ=0 EndX=-19 EndY=10 EndZ=0
    g2: LineSegment StartX=-16.994 StartY=21.7049 StartZ=0 EndX=-11 EndY=10 EndZ=0
    g3: LineSegment StartX=-22.4581 StartY=20.2408 StartZ=0 EndX=-16.994 EndY=21.7049 EndZ=0
  constraints (8):
    c: Coincident(g0,g-5)
    c: Coincident(g0,g-3)
    c: Coincident(g1,g0)
    c: Coincident(g2,g-6)
    c: Coincident(g2,g1)
    c: Coincident(g3,g0)
    c: Coincident(g3,g2)
    c: Coincident(g1,g-5)
FEATURE [Part::Extrusion] Extrude025
  Base = -> Sketch024
  Dir = (-1,0,0)
  DirMode = 2
  FaceMakerClass = Part::FaceMakerBullseye
  LengthFwd = 4
  LengthRev = 0
  Reversed = true
  Solid = true
  Symmetric = false
FEATURE [Part::FeaturePython] Connect006  label="Pin_Reset"  # WARN: FeaturePython — macro-defined, semantics opaque (R4)
  Objects = -> [Extrude024,Extrude025]
  Tolerance = 0
FEATURE [Mesh::Feature] Mesh006  label="Pin_Boot (Meshed)"
FEATURE [Mesh::Feature] Mesh007  label="Pin_Reset (Meshed)"
